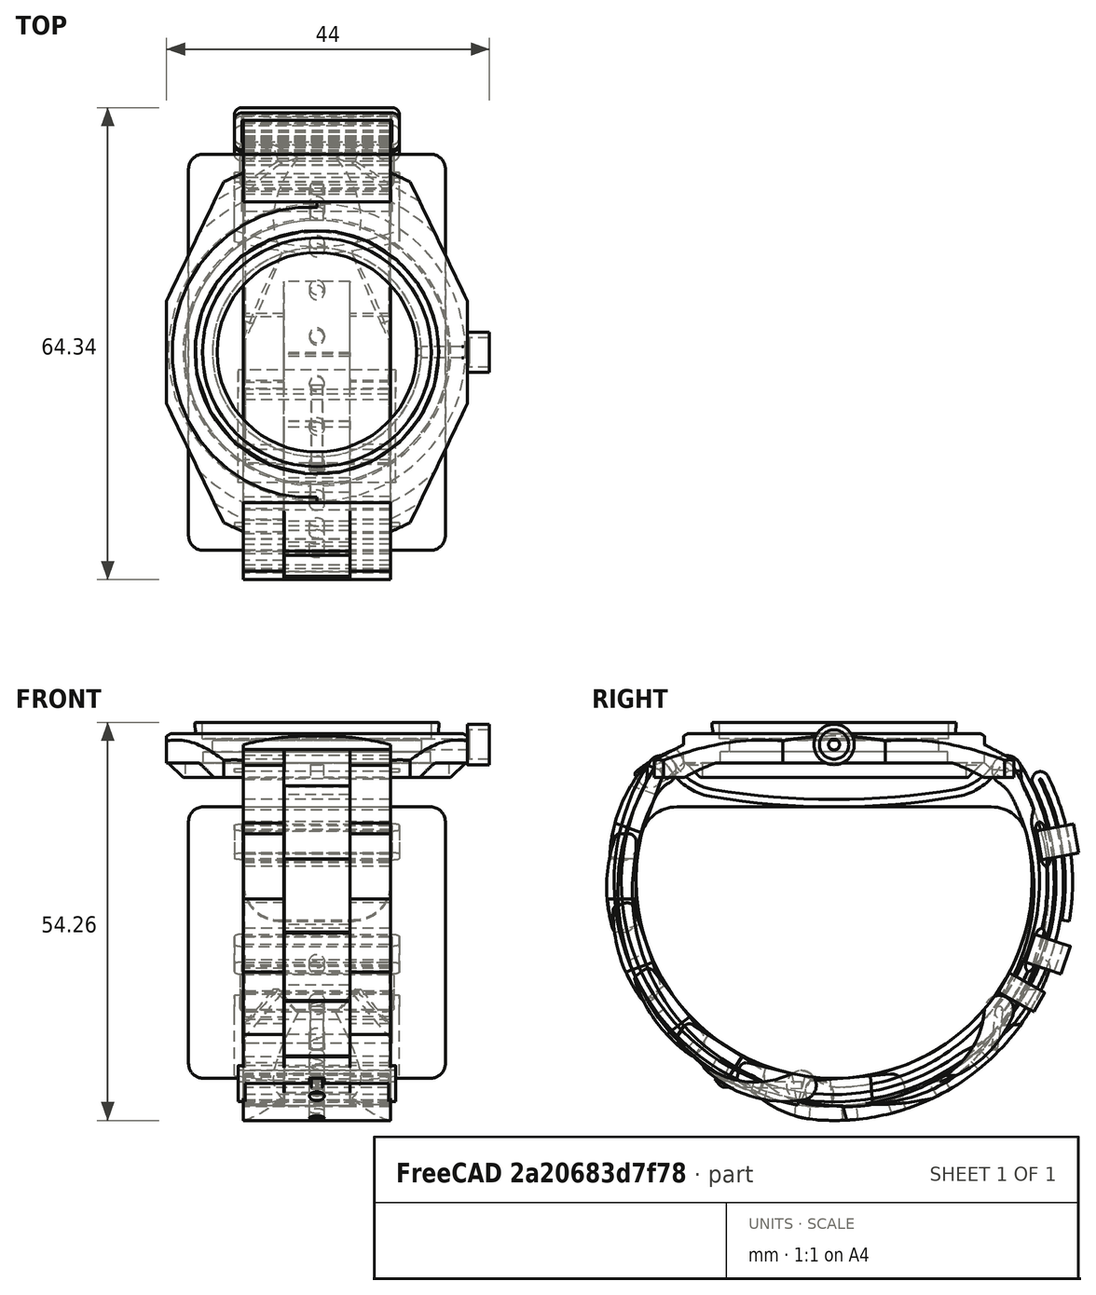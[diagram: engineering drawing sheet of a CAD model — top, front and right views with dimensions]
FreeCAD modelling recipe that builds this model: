
FCSTD DOCUMENT  (FreeCAD 0.19R20415 (Git))
Label: Strap_2
License: All rights reserved
LicenseURL: http://en.wikipedia.org/wiki/All_rights_reserved
objects: Sketcher::SketchObject×36, PartDesign::Pad×14, PartDesign::Body×14, PartDesign::Pocket×11, PartDesign::Plane×7, PartDesign::Fillet×6, PartDesign::SubtractivePipe×5, PartDesign::Mirrored×5, PartDesign::ShapeBinder×3, App::DocumentObjectGroup×3, Mesh::Feature×2, Part::FeaturePython×2, Part::Feature×1, Part::Cylinder×1, Spreadsheet::Sheet×1, PartDesign::Point×1, Part::Cut×1
note: 143 computed .brp shape members not serialized (recipe doc carries the construction recipe); baked Part::Feature solids carry a one-line shape summary decoded from their .brp

FEATURE [Mesh::Feature] hand_01
  Placement = pos=(-135.279,-150.508,-37.6643) rot=(-0.520735,-0.542376,-0.65929;2.00353rad)
FEATURE [Sketcher::SketchObject] Sketch030
  MapMode = 5
  Placement = pos=(0,0,0) rot=(0.57735,0.57735,0.57735;2.0944rad)
  Support = -> [YZ_Plane002]
  sketch-geometry (5):
    g0: ArcOfCircle CenterX=0 CenterY=-10 CenterZ=0 NormalX=0 NormalY=0 NormalZ=1 AngleXU=0 Radius=27 StartAngle=2.91232 EndAngle=6.51246
    g1: GeomPoint X=0 Y=0 Z=0
    g2: LineSegment StartX=-21.4243 StartY=0 StartZ=0 EndX=21.4243 EndY=0 EndZ=0
    g3: ArcOfCircle CenterX=21.4243 CenterY=-5 CenterZ=0 NormalX=0 NormalY=0 NormalZ=1 AngleXU=0 Radius=5 StartAngle=0.229276 EndAngle=1.5708
    g4: ArcOfCircle CenterX=-21.4243 CenterY=-5 CenterZ=0 NormalX=0 NormalY=0 NormalZ=1 AngleXU=0 Radius=5 StartAngle=1.5708 EndAngle=2.91232
  constraints (12):
    c: PointOnObject(g0,g-2)
    c: Coincident(g1,g-1)
    c: Radius(g0) = 27
    c: Horizontal(g2)
    c: PointOnObject(g1,g2)
    c: DistanceY(g0,g1) = 10
    c: Tangent(g0,g3) = -1.5708
    c: Tangent(g2,g3) = 1.5708
    c: Tangent(g0,g4) = -1.5708
    c: Tangent(g2,g4) = 1.5708
    c: Equal(g4,g3)
    c: Radius(g3) = 5
FEATURE [PartDesign::Pad] Pad002
  Length = 35
  Length2 = 100
  Midplane = true
  Placement = pos=(0,0,0) rot=(0.57735,0.57735,0.57735;2.0944rad)
  Profile = -> Sketch030
  Type = 0
FEATURE [Sketcher::SketchObject] Sketch031
  MapMode = 5
  Placement = pos=(0,0,0) rot=(0.57735,0.57735,0.57735;2.0944rad)
  Support = -> [YZ_Plane001]
  expr: Constraints[7] = Spreadsheet.Haut
  expr: Constraints[25] = Spreadsheet.EpaisNato
  expr: Constraints[122] = Spreadsheet.EntreAxe
  sketch-geometry (53):
    g0: ArcOfCircle CenterX=0 CenterY=-10.2233 CenterZ=0 NormalX=0 NormalY=0 NormalZ=1 AngleXU=0 Radius=30 StartAngle=2.56676 EndAngle=5.32325
    g1: ArcOfCircle CenterX=1.77e-14 CenterY=101 CenterZ=0 NormalX=0 NormalY=0 NormalZ=1 AngleXU=0 Radius=100 StartAngle=4.54638 EndAngle=4.8784
    g2: ArcOfCircle CenterX=-23.5 CenterY=5 CenterZ=0 NormalX=0 NormalY=0 NormalZ=1 AngleXU=0 Radius=2 StartAngle=0.526234 EndAngle=2.56676
    g3: ArcOfCircle CenterX=-15.2853 CenterY=9.77166 CenterZ=0 NormalX=0 NormalY=0 NormalZ=1 AngleXU=0 Radius=7.5 StartAngle=3.66783 EndAngle=4.54638
    g4: GeomPoint X=0 Y=1 Z=0
    g5: LineSegment [constr] StartX=17.2073 StartY=-34.7979 StartZ=0 EndX=0 EndY=-10.2233 EndZ=0
    g6: ArcOfCircle CenterX=15.2853 CenterY=9.77166 CenterZ=0 NormalX=0 NormalY=0 NormalZ=1 AngleXU=0 Radius=7.5 StartAngle=4.8784 EndAngle=5.75695
    g7: ArcOfCircle CenterX=23.5 CenterY=5 CenterZ=0 NormalX=0 NormalY=0 NormalZ=1 AngleXU=0 Radius=2 StartAngle=0.574828 EndAngle=2.61536
    g8: ArcOfCircle CenterX=0 CenterY=-10.2233 CenterZ=0 NormalX=0 NormalY=0 NormalZ=1 AngleXU=0 Radius=30 StartAngle=5.62307 EndAngle=6.85801
    g9: ArcOfCircle CenterX=0 CenterY=-10.2233 CenterZ=0 NormalX=0 NormalY=0 NormalZ=1 AngleXU=0 Radius=29 StartAngle=0.347744 EndAngle=0.574828
    g10: LineSegment [constr] StartX=27.2642 StartY=-0.340778 StartZ=0 EndX=28.2043 EndY=0 EndZ=0
    g11: ArcOfCircle CenterX=15.2853 CenterY=9.77166 CenterZ=0 NormalX=0 NormalY=0 NormalZ=1 AngleXU=0 Radius=8.5 StartAngle=4.8784 EndAngle=5.75695
    g12: LineSegment [constr] StartX=16.5247 StartY=2.37477 StartZ=0 EndX=16.6899 EndY=1.38852 EndZ=0
    g13: ArcOfCircle CenterX=1.77e-14 CenterY=101 CenterZ=0 NormalX=0 NormalY=0 NormalZ=1 AngleXU=0 Radius=101 StartAngle=4.54638 EndAngle=4.8784
    g14: ArcOfCircle CenterX=-15.2853 CenterY=9.77166 CenterZ=0 NormalX=0 NormalY=0 NormalZ=1 AngleXU=0 Radius=8.5 StartAngle=3.66783 EndAngle=4.54638
    g15: ArcOfCircle CenterX=-23.5 CenterY=5 CenterZ=0 NormalX=0 NormalY=0 NormalZ=1 AngleXU=0 Radius=1 StartAngle=0.526234 EndAngle=2.56676
    g16: LineSegment [constr] StartX=-16.6899 StartY=1.38852 StartZ=0 EndX=-16.5247 EndY=2.37477 EndZ=0
    g17: LineSegment [constr] StartX=-22.6353 StartY=5.50228 StartZ=0 EndX=-21.7706 EndY=6.00456 EndZ=0
    g18: ArcOfCircle CenterX=0 CenterY=-10.2233 CenterZ=0 NormalX=0 NormalY=0 NormalZ=1 AngleXU=0 Radius=29 StartAngle=2.56676 EndAngle=5.32325
    g19: LineSegment [constr] StartX=-24.3393 StartY=5.54369 StartZ=0 EndX=-25.1786 EndY=6.08738 EndZ=0
    g20: ArcOfCircle CenterX=23.5 CenterY=5 CenterZ=0 NormalX=0 NormalY=0 NormalZ=1 AngleXU=0 Radius=1 StartAngle=0.574828 EndAngle=2.61536
    g21: ArcOfCircle CenterX=0 CenterY=-10.2233 CenterZ=0 NormalX=0 NormalY=0 NormalZ=1 AngleXU=0 Radius=28 StartAngle=5.62307 EndAngle=6.54195
    g22: LineSegment [constr] StartX=22.1178 StartY=-27.3931 StartZ=0 EndX=22.9077 EndY=-28.0063 EndZ=0
    g23: ArcOfCircle CenterX=22.9077 CenterY=-28.0063 CenterZ=0 NormalX=0 NormalY=0 NormalZ=1 AngleXU=0 Radius=1 StartAngle=2.48148 EndAngle=5.62307
    g24: ArcOfCircle CenterX=24.6758 CenterY=-45.4641 CenterZ=0 NormalX=0 NormalY=0 NormalZ=1 AngleXU=0 Radius=14.021 StartAngle=2.01355 EndAngle=2.18166
    g25: ArcOfCircle CenterX=12.0856 CenterY=-18.9105 CenterZ=0 NormalX=0 NormalY=0 NormalZ=1 AngleXU=0 Radius=15.3662 StartAngle=5.15514 EndAngle=5.65995
    g26: ArcOfCircle CenterX=0 CenterY=-10.2233 CenterZ=0 NormalX=0 NormalY=0 NormalZ=1 AngleXU=0 Radius=30.25 StartAngle=5.65995 EndAngle=6.74266
    g27: ArcOfCircle CenterX=28.121 CenterY=3.69067 CenterZ=0 NormalX=0 NormalY=0 NormalZ=1 AngleXU=0 Radius=1.125 StartAngle=0.459471 EndAngle=3.60106
    g28: ArcOfCircle CenterX=0 CenterY=-10.2233 CenterZ=0 NormalX=0 NormalY=0 NormalZ=1 AngleXU=0 Radius=32.5 StartAngle=6.11712 EndAngle=6.74266
    g29: LineSegment [constr] StartX=27.1127 StartY=3.19176 StartZ=0 EndX=29.1293 EndY=4.18958 EndZ=0
    g30: ArcOfCircle CenterX=24.6758 CenterY=-45.4641 CenterZ=0 NormalX=0 NormalY=0 NormalZ=1 AngleXU=0 Radius=13.021 StartAngle=2.01355 EndAngle=2.18166
    g31: ArcOfCircle CenterX=12.0856 CenterY=-18.9105 CenterZ=0 NormalX=0 NormalY=0 NormalZ=1 AngleXU=0 Radius=16.3662 StartAngle=5.15514 EndAngle=5.65995
    g32: ArcOfCircle CenterX=0 CenterY=-10.2233 CenterZ=0 NormalX=0 NormalY=0 NormalZ=1 AngleXU=0 Radius=31.25 StartAngle=5.65995 EndAngle=6.74266
    g33: ArcOfCircle CenterX=28.121 CenterY=3.69067 CenterZ=0 NormalX=0 NormalY=0 NormalZ=1 AngleXU=0 Radius=0.125 StartAngle=0.459471 EndAngle=3.60106
    g34: ArcOfCircle CenterX=0 CenterY=-10.2233 CenterZ=0 NormalX=0 NormalY=0 NormalZ=1 AngleXU=0 Radius=31.5 StartAngle=6.11712 EndAngle=6.74266
    g35: LineSegment StartX=31.0667 StartY=-15.4303 StartZ=0 EndX=32.0529 EndY=-15.5956 EndZ=0
    g36: LineSegment [constr] StartX=28.009 StartY=3.63524 StartZ=0 EndX=27.1127 EndY=3.19176 EndZ=0
    g37: LineSegment [constr] StartX=28.2043 StartY=0 StartZ=0 EndX=28.4394 EndY=0.0851945 EndZ=0
    g38: ArcOfCircle CenterX=31.1215 CenterY=-1.98547 CenterZ=0 NormalX=0 NormalY=0 NormalZ=1 AngleXU=0 Radius=4.19336 StartAngle=2.73856 EndAngle=3.40036
    g39: LineSegment StartX=27.5841 StartY=-3.40486 StartZ=0 EndX=28.2879 EndY=-7.54548 EndZ=0
    g40: LineSegment StartX=28.2879 StartY=-7.54548 StartZ=0 EndX=29.4709 EndY=-7.3444 EndZ=0
    g41: LineSegment StartX=29.4709 StartY=-7.3444 StartZ=0 EndX=28.7671 EndY=-3.20378 EndZ=0
    g42: LineSegment StartX=28.7671 StartY=-3.20378 StartZ=0 EndX=27.5841 EndY=-3.40486 EndZ=0
    g43: LineSegment [constr] StartX=0 StartY=-10.2233 StartZ=0 EndX=29.119 EndY=-5.27409 EndZ=0
    g44: LineSegment StartX=27.5164 StartY=-17.3102 StartZ=0 EndX=26.1711 EndY=-21.289 EndZ=0
    g45: LineSegment StartX=26.1711 StartY=-21.289 StartZ=0 EndX=27.3079 EndY=-21.6733 EndZ=0
    g46: LineSegment StartX=27.3079 StartY=-21.6733 StartZ=0 EndX=28.6531 EndY=-17.6946 EndZ=0
    g47: LineSegment StartX=28.6531 StartY=-17.6946 StartZ=0 EndX=27.5164 EndY=-17.3102 EndZ=0
    g48: LineSegment [constr] StartX=0 StartY=-10.2233 StartZ=0 EndX=27.9805 EndY=-19.684 EndZ=0
    g49: Circle [constr] CenterX=0 CenterY=-10.2233 CenterZ=0 NormalX=0 NormalY=0 NormalZ=1 AngleXU=0 Radius=29.6112
    g50: LineSegment [constr] StartX=29.119 StartY=-5.27409 StartZ=0 EndX=29.5758 EndY=-5.19645 EndZ=0
    g51: LineSegment [constr] StartX=28.7671 StartY=-3.20378 StartZ=0 EndX=29.1514 EndY=-3.13847 EndZ=0
    g52: LineSegment [constr] StartX=27.5841 StartY=-3.40486 StartZ=0 EndX=27.1998 EndY=-3.47017 EndZ=0
  constraints (131):
    c: Symmetric(g1,g1,g-2)
    c: Tangent(g2,g0) = -1.5708
    c: Radius(g2) = 2
    c: Tangent(g1,g3) = -1.5708
    c: Tangent(g3,g2) = 1.5708
    c: Radius(g0) = 30
    c: Radius(g3) = 7.5
    c: DistanceY(g2) = 5
    c: PointOnObject(g4,g1)
    c: PointOnObject(g4,g-2)
    c: Radius(g1) = 100
    c: PointOnObject(g0,g-2)
    c: Coincident(g5,g0)
    c: Coincident(g5,g0)
    c: Angle(g5,g-2) = 2.53073
    c: Tangent(g6,g1) = -1.5708
    c: Symmetric(g6,g2,g-2)
    c: Tangent(g7,g6) = 1.5708
    c: Equal(g7,g2)
    c: Coincident(g8,g0)
    c: Tangent(g8,g7) = -1.5708
    c: Coincident(g9,g0)
    c: Coincident(g10,g9)
    c: PointOnObject(g10,g8)
    c: Perpendicular(g8,g10)
    c: Distance(g10) = 1
    c: Coincident(g12,g1)
    c: Perpendicular(g11,g12)
    c: Equal(g10,g12)
    c: Coincident(g13,g1)
    c: Tangent(g11,g13) = -1.5708
    c: Perpendicular(g6,g12)
    c: Tangent(g13,g14) = -1.5708
    c: Coincident(g16,g13)
    c: Coincident(g16,g1)
    c: Perpendicular(g13,g16)
    c: Equal(g16,g12)
    c: Tangent(g15,g14) = 1.5708
    c: Coincident(g17,g14)
    c: PointOnObject(g17,g3)
    c: Perpendicular(g3,g17)
    c: Equal(g17,g16)
    c: Coincident(g18,g0)
    c: Tangent(g18,g15) = -1.5708
    c: Coincident(g19,g15)
    c: Perpendicular(g0,g19)
    c: Equal(g19,g17)
    c: Coincident(g15,g2)
    c: Coincident(g20,g7)
    c: Tangent(g11,g20) = 1.5708
    c: Tangent(g9,g20) = -1.5708
    c: Coincident(g21,g0)
    c: Coincident(g22,g21)
    c: Equal(g22,g10)
    c: Tangent(g23,g21) = 1.5708
    c: Coincident(g23,g22)
    c: Tangent(g24,g18) = 1.5708
    c: Tangent(g25,g24) = 1.5708
    c: Coincident(g26,g0)
    c: Coincident(g26,g25)
    c: Coincident(g28,g0)
    c: Tangent(g27,g26) = 1.5708
    c: Tangent(g27,g28) = -1.5708
    c: Coincident(g29,g26)
    c: Coincident(g29,g27)
    c: Coincident(g30,g24)
    c: Coincident(g31,g25)
    c: Coincident(g32,g0)
    c: Tangent(g30,g0) = 1.5708
    c: Tangent(g30,g31) = 1.5708
    c: Tangent(g31,g32) = -1.5708
    c: Tangent(g32,g33) = 1.5708
    c: Coincident(g34,g0)
    c: Tangent(g34,g33) = -1.5708
    c: Coincident(g35,g34)
    c: Coincident(g35,g28)
    c: Perpendicular(g34,g35)
    c: Equal(g35,g10)
    c: Coincident(g36,g32)
    c: Perpendicular(g32,g36)
    c: Equal(g36,g10)
    c: Distance(g32,g33) = 0.25
    c: Coincident(g27,g33)
    c: Coincident(g37,g10)
    c: PointOnObject(g37,g26)
    c: Perpendicular(g26,g37)
    c: Distance(g37) = 0.25
    c: Tangent(g38,g21) = 1.5708
    c: Coincident(g9,g38)
    c: Distance(g27,g28) = 20
    c: PointOnObject(g10,g-1)
    c: Tangent(g23,g8) = -1.5708
    c: Coincident(g39,g40)
    c: Coincident(g40,g41)
    c: Coincident(g41,g42)
    c: Coincident(g42,g39)
    c: Perpendicular(g41,g40)
    c: Perpendicular(g41,g42)
    c: Perpendicular(g42,g39)
    c: Distance(g40) = 1.2
    c: Distance(g41) = 4.2
    c: Coincident(g43,g0)
    c: Perpendicular(g43,g41)
    c: Symmetric(g40,g41,g43)
    c: Coincident(g44,g45)
    c: Coincident(g45,g46)
    c: Coincident(g46,g47)
    c: Coincident(g47,g44)
    c: Perpendicular(g46,g45)
    c: Perpendicular(g46,g47)
    c: Perpendicular(g47,g44)
    c: Equal(g40,g45) = 1.2
    c: Equal(g41,g46) = 4.2
    c: Coincident(g48,g0)
    c: Perpendicular(g46,g48)
    c: Symmetric(g45,g46,g48)
    c: Coincident(g49,g0)
    c: PointOnObject(g40,g49)
    c: PointOnObject(g46,g49)
    c: Coincident(g50,g43)
    c: PointOnObject(g50,g8)
    c: Parallel(g50,g43)
    c: DistanceX(g2,g7) = 47
    c: Coincident(g51,g41)
    c: PointOnObject(g51,g8)
    c: Coincident(g52,g39)
    c: PointOnObject(g52,g38)
    c: Parallel(g52,g42)
    c: Parallel(g51,g42)
    c: Equal(g51,g52)
    c: PointOnObject(g-1,g13)
FEATURE [Part::Feature] Body003  label="K-65_Case001"
  shape: bbox 50.12 x 59.75 x 8.013 mm, 71 faces (baked)
FEATURE [PartDesign::Pad] Pad
  Length = 20
  Length2 = 100
  Midplane = true
  Placement = pos=(0,0,0) rot=(0.57735,0.57735,0.57735;2.0944rad)
  Profile = -> Sketch031
  Type = 0
  expr: Length = Spreadsheet.Larg
FEATURE [Sketcher::SketchObject] Sketch
  MapMode = 5
  Placement = pos=(0,0,0) rot=(0.57735,0.57735,0.57735;2.0944rad)
  Support = -> [YZ_Plane]
  expr: Constraints[10] = Spreadsheet.EpaisNato * 3 + 2.1
  sketch-geometry (7):
    g0: LineSegment StartX=27.6094 StartY=-3.26258 StartZ=0 EndX=32.6253 EndY=-2.34006 EndZ=0
    g1: LineSegment StartX=32.6253 StartY=-2.34006 StartZ=0 EndX=33.3488 EndY=-6.27408 EndZ=0
    g2: LineSegment StartX=33.3488 StartY=-6.27408 StartZ=0 EndX=28.333 EndY=-7.19659 EndZ=0
    g3: LineSegment StartX=27.6094 StartY=-3.26258 StartZ=0 EndX=28.333 EndY=-7.19659 EndZ=0
    g4: LineSegment [constr] StartX=27.9712 StartY=-5.22959 StartZ=0 EndX=32.9871 EndY=-4.30707 EndZ=0
    g5: LineSegment [constr] StartX=27.6094 StartY=-3.26258 StartZ=0 EndX=27.5111 EndY=-3.28067 EndZ=0
    g6: LineSegment [constr] StartX=27.6094 StartY=-3.26258 StartZ=0 EndX=27.5913 EndY=-3.16423 EndZ=0
  constraints (17):
    c: Coincident(g0,g1)
    c: Coincident(g1,g2)
    c: Coincident(g0,g3)
    c: Coincident(g3,g2)
    c: Perpendicular(g0,g3)
    c: Perpendicular(g1,g2)
    c: Perpendicular(g0,g1)
    c: Distance(g3) = 4
    c: Symmetric(g0,g1,g4)
    c: Symmetric(g0,g2,g4)
    c: Distance(g2) = 5.1
    c: Coincident(g5,g0)
    c: Coincident(g6,g0)
    c: Parallel(g0,g5)
    c: Parallel(g6,g3)
    c: Equal(g6,g5)
    c: Distance(g6) = 0.1
FEATURE [PartDesign::Pad] Pad003
  Length = 22.5
  Length2 = 100
  Midplane = true
  Placement = pos=(0,0,0) rot=(0.57735,0.57735,0.57735;2.0944rad)
  Profile = -> Sketch
  Type = 0
  expr: Length = Spreadsheet.Larg + 2.5
FEATURE [Sketcher::SketchObject] Sketch032
  ExternalGeometry = -> [Pad003]
  MapMode = 5
  Placement = pos=(2.9e-15,1.48379,-8.06759) rot=(0.090446,0.090446,-0.991786;1.57904rad)
  Support = -> [Pad003]
  sketch-geometry (11):
    g0: LineSegment StartX=-30.4638 StartY=10.25 StartZ=0 EndX=-27.7638 EndY=10.25 EndZ=0
    g1: LineSegment StartX=-27.5638 StartY=10.05 StartZ=0 EndX=-27.5638 EndY=-10.05 EndZ=0
    g2: LineSegment StartX=-27.7638 StartY=-10.25 StartZ=0 EndX=-30.4638 EndY=-10.25 EndZ=0
    g3: LineSegment StartX=-30.6638 StartY=-10.05 StartZ=0 EndX=-30.6638 EndY=10.05 EndZ=0
    g4: GeomPoint X=-29.1138 Y=4.1e-15 Z=0
    g5: ArcOfCircle CenterX=-30.4638 CenterY=10.05 CenterZ=0 NormalX=0 NormalY=0 NormalZ=1 AngleXU=0 Radius=0.2 StartAngle=1.5708 EndAngle=3.14159
    g6: ArcOfCircle CenterX=-27.7638 CenterY=10.05 CenterZ=0 NormalX=0 NormalY=0 NormalZ=1 AngleXU=0 Radius=0.2 StartAngle=-3.6e-15 EndAngle=1.5708
    g7: ArcOfCircle CenterX=-27.7638 CenterY=-10.05 CenterZ=0 NormalX=0 NormalY=0 NormalZ=1 AngleXU=0 Radius=0.2 StartAngle=4.71239 EndAngle=6.28319
    g8: ArcOfCircle CenterX=-30.4638 CenterY=-10.05 CenterZ=0 NormalX=0 NormalY=0 NormalZ=1 AngleXU=0 Radius=0.2 StartAngle=3.14159 EndAngle=4.71239
    g9: LineSegment [constr] StartX=-30.4638 StartY=-10.25 StartZ=0 EndX=-30.4638 EndY=-11.25 EndZ=0
    g10: LineSegment [constr] StartX=-30.6638 StartY=-10.05 StartZ=0 EndX=-31.6638 EndY=-10.05 EndZ=0
  constraints (26):
    c: Horizontal(g0)
    c: Horizontal(g2)
    c: Vertical(g1)
    c: Vertical(g3)
    c: Symmetric(g-4,g-3,g4)
    c: Tangent(g3,g5) = 1.5708
    c: Tangent(g0,g5) = 1.5708
    c: Tangent(g0,g6) = 1.5708
    c: Tangent(g1,g6) = 1.5708
    c: Tangent(g1,g7) = 1.5708
    c: Tangent(g2,g7) = 1.5708
    c: Tangent(g2,g8) = 1.5708
    c: Tangent(g3,g8) = 1.5708
    c: Equal(g8,g7)
    c: Equal(g7,g5)
    c: Equal(g5,g6)
    c: Radius(g5) = 0.2
    c: DistanceY(g-4,g2) = 1
    c: Coincident(g9,g2)
    c: Coincident(g10,g3)
    c: PointOnObject(g10,g-4)
    c: Horizontal(g10)
    c: Horizontal(g9,g-4)
    c: Vertical(g9)
    c: Equal(g10,g9)
    c: Symmetric(g7,g5,g4)
FEATURE [PartDesign::Pocket] Pocket
  BaseFeature = -> Pad003
  Length = 5
  Length2 = 100
  Placement = pos=(0,0,0) rot=(0.57735,0.57735,0.57735;2.0944rad)
  Profile = -> Sketch032
  Type = 0
FEATURE [PartDesign::Fillet] Fillet001
  Base = -> Pocket [Edge18,Edge15,Edge16,Edge14]
  BaseFeature = -> Pocket
  Placement = pos=(0,0,0) rot=(0.57735,0.57735,0.57735;2.0944rad)
  Radius = 1
  SupportTransform = true
FEATURE [PartDesign::Body] Body  label="Nato_Retainer_1"
  Group = -> [Sketch,Pad003,Sketch032,Pocket,Fillet001]
  Origin = -> Origin
  Tip = -> Fillet001
FEATURE [PartDesign::ShapeBinder] ShapeBinder001
  Placement = pos=(10,-4e-15,4e-15) rot=(0,0,1;0rad)
  TraceSupport = false
FEATURE [Sketcher::SketchObject] Sketch033
  ExternalGeometry = -> [ShapeBinder001]
  MapMode = 5
  Placement = pos=(0,0,0) rot=(0.57735,0.57735,0.57735;2.0944rad)
  Support = -> [YZ_Plane003]
  expr: Constraints[7] = Spreadsheet.EpaisNato * 3 + 2.1
  sketch-geometry (6):
    g0: LineSegment StartX=27.3747 StartY=-17.38 StartZ=0 EndX=32.2053 EndY=-19.0156 EndZ=0
    g1: LineSegment StartX=32.2053 StartY=-19.0156 StartZ=0 EndX=30.9226 EndY=-22.8043 EndZ=0
    g2: LineSegment StartX=30.9226 StartY=-22.8043 StartZ=0 EndX=26.0919 EndY=-21.1688 EndZ=0
    g3: LineSegment StartX=26.0919 StartY=-21.1688 StartZ=0 EndX=27.3747 EndY=-17.38 EndZ=0
    g4: LineSegment [constr] StartX=27.3747 StartY=-17.38 StartZ=0 EndX=27.4068 EndY=-17.2853 EndZ=0
    g5: LineSegment [constr] StartX=27.3747 StartY=-17.38 StartZ=0 EndX=27.4694 EndY=-17.4121 EndZ=0
  constraints (18):
    c: Coincident(g0,g1)
    c: Coincident(g1,g2)
    c: Coincident(g2,g3)
    c: Coincident(g3,g0)
    c: Perpendicular(g0,g3)
    c: Perpendicular(g2,g3)
    c: Perpendicular(g1,g2)
    c: Distance(g2) = 5.1
    c: Distance(g3) = 4
    c: Parallel(g3,g-5)
    c: Coincident(g4,g0)
    c: PointOnObject(g4,g-4)
    c: PointOnObject(g5,g-5)
    c: Coincident(g5,g0)
    c: Parallel(g5,g0)
    c: Parallel(g4,g3)
    c: Equal(g4,g5)
    c: Distance(g4) = 0.1
FEATURE [PartDesign::Pad] Pad004
  Length = 22.5
  Length2 = 100
  Midplane = true
  Placement = pos=(0,0,0) rot=(0.57735,0.57735,0.57735;2.0944rad)
  Profile = -> Sketch033
  Type = 0
  expr: Length = Spreadsheet.Larg + 2.5
FEATURE [Sketcher::SketchObject] Sketch034
  ExternalGeometry = -> [Pad004]
  MapMode = 5
  Placement = pos=(9e-16,-2.46397,-7.27759) rot=(-0.1604,-0.1604,-0.973932;1.59721rad)
  Support = -> [Pad004]
  sketch-geometry (11):
    g0: LineSegment StartX=-35.4025 StartY=10.25 StartZ=0 EndX=-32.7025 EndY=10.25 EndZ=0
    g1: LineSegment StartX=-32.5025 StartY=10.05 StartZ=0 EndX=-32.5025 EndY=-10.05 EndZ=0
    g2: LineSegment StartX=-32.7025 StartY=-10.25 StartZ=0 EndX=-35.4025 EndY=-10.25 EndZ=0
    g3: LineSegment StartX=-35.6025 StartY=-10.05 StartZ=0 EndX=-35.6025 EndY=10.05 EndZ=0
    g4: GeomPoint X=-34.0525 Y=5e-15 Z=0
    g5: ArcOfCircle CenterX=-35.4025 CenterY=10.05 CenterZ=0 NormalX=0 NormalY=0 NormalZ=1 AngleXU=0 Radius=0.2 StartAngle=1.5708 EndAngle=3.14159
    g6: ArcOfCircle CenterX=-32.7025 CenterY=10.05 CenterZ=0 NormalX=0 NormalY=0 NormalZ=1 AngleXU=0 Radius=0.2 StartAngle=-4.4e-15 EndAngle=1.5708
    g7: ArcOfCircle CenterX=-32.7025 CenterY=-10.05 CenterZ=0 NormalX=0 NormalY=0 NormalZ=1 AngleXU=0 Radius=0.2 StartAngle=4.71239 EndAngle=6.28319
    g8: ArcOfCircle CenterX=-35.4025 CenterY=-10.05 CenterZ=0 NormalX=0 NormalY=0 NormalZ=1 AngleXU=0 Radius=0.2 StartAngle=3.14159 EndAngle=4.71239
    g9: LineSegment [constr] StartX=-35.4025 StartY=10.25 StartZ=0 EndX=-35.4025 EndY=11.25 EndZ=0
    g10: LineSegment [constr] StartX=-35.6025 StartY=10.05 StartZ=0 EndX=-36.6025 EndY=10.05 EndZ=0
  constraints (26):
    c: Horizontal(g0)
    c: Horizontal(g2)
    c: Vertical(g1)
    c: Vertical(g3)
    c: Tangent(g3,g5) = 1.5708
    c: Tangent(g0,g5) = 1.5708
    c: Tangent(g0,g6) = 1.5708
    c: Tangent(g1,g6) = 1.5708
    c: Tangent(g1,g7) = 1.5708
    c: Tangent(g2,g7) = 1.5708
    c: Tangent(g2,g8) = 1.5708
    c: Tangent(g3,g8) = 1.5708
    c: Equal(g8,g7)
    c: Equal(g7,g5)
    c: Equal(g5,g6)
    c: Radius(g5) = 0.2
    c: Symmetric(g7,g5,g4)
    c: Symmetric(g-5,g-4,g4)
    c: Coincident(g9,g0)
    c: Vertical(g9)
    c: Coincident(g10,g3)
    c: PointOnObject(g10,g-4)
    c: Horizontal(g10)
    c: PointOnObject(g9,g-3)
    c: Equal(g9,g10)
    c: DistanceX(g10,g10) = 1
FEATURE [PartDesign::Pocket] Pocket001
  BaseFeature = -> Pad004
  Length = 5
  Length2 = 100
  Placement = pos=(0,0,0) rot=(0.57735,0.57735,0.57735;2.0944rad)
  Profile = -> Sketch034
  Type = 0
FEATURE [PartDesign::Fillet] Fillet002
  Base = -> Pocket001 [Edge18,Edge15,Edge16,Edge14]
  BaseFeature = -> Pocket001
  Placement = pos=(0,0,0) rot=(0.57735,0.57735,0.57735;2.0944rad)
  Radius = 1
  SupportTransform = true
FEATURE [PartDesign::Body] Body004  label="Nato_Retainer_2"
  Group = -> [ShapeBinder001,Sketch033,Pad004,Sketch034,Pocket001,Fillet002]
  Origin = -> Origin003
  Tip = -> Fillet002
FEATURE [Sketcher::SketchObject] Sketch035
  MapMode = 5
  Placement = pos=(0,0,0) rot=(0.57735,0.57735,0.57735;2.0944rad)
  Support = -> [YZ_Plane004]
  sketch-geometry (7):
    g0: ArcOfCircle CenterX=8.92707 CenterY=-26.8072 CenterZ=0 NormalX=0 NormalY=0 NormalZ=1 AngleXU=0 Radius=11.6054 StartAngle=5.10639 EndAngle=6.21654
    g1: ArcOfCircle CenterX=22.5023 CenterY=-27.7132 CenterZ=0 NormalX=0 NormalY=0 NormalZ=1 AngleXU=0 Radius=2 StartAngle=5.8952 EndAngle=9.35814
    g2: ArcOfCircle CenterX=10.0199 CenterY=-22.6117 CenterZ=0 NormalX=0 NormalY=0 NormalZ=1 AngleXU=0 Radius=15.4846 StartAngle=4.93527 EndAngle=5.8952
    g3: ArcOfCircle CenterX=13.4206 CenterY=-37.6158 CenterZ=0 NormalX=0 NormalY=0 NormalZ=1 AngleXU=0 Radius=0.1 StartAngle=1.96479 EndAngle=4.93527
    g4: GeomPoint X=22.6355 Y=-25.7177 Z=0
    g5: LineSegment [constr] StartX=22.6355 StartY=-25.7177 StartZ=0 EndX=22.5023 EndY=-27.7132 EndZ=0
    g6: LineSegment [constr] StartX=20.5067 StartY=-27.58 StartZ=0 EndX=22.5023 EndY=-27.7132 EndZ=0
  constraints (14):
    c: Tangent(g0,g1) = 1.5708
    c: Tangent(g2,g1) = -1.5708
    c: Tangent(g3,g0) = 1.5708
    c: Tangent(g3,g2) = -1.5708
    c: Radius(g3) = 0.1
    c: Radius(g1) = 2
    c: Angle(g2) = 0.959931
    c: PointOnObject(g4,g1)
    c: Coincident(g5,g4)
    c: Coincident(g5,g1)
    c: Coincident(g6,g0)
    c: Coincident(g6,g1)
    c: Perpendicular(g6,g5)
    c: Distance(g4,g0) = 15
FEATURE [PartDesign::Pad] Pad005
  Length = 22.5
  Length2 = 100
  Midplane = true
  Placement = pos=(0,0,0) rot=(0.57735,0.57735,0.57735;2.0944rad)
  Profile = -> Sketch035
  Type = 0
  expr: Length = Spreadsheet.Larg + 2.5
FEATURE [Sketcher::SketchObject] Sketch036
  ExternalGeometry = -> [Pad005]
  MapMode = 5
  Placement = pos=(0,0,0) rot=(1,0,0;1.5708rad)
  Support = -> [XZ_Plane004]
  sketch-geometry (10):
    g0: LineSegment StartX=-10.25 StartY=-25.58 StartZ=0 EndX=10.25 EndY=-25.58 EndZ=0
    g1: LineSegment StartX=10.25 StartY=-25.58 StartZ=0 EndX=10.25 EndY=-32.2133 EndZ=0
    g2: LineSegment StartX=10.25 StartY=-32.2133 StartZ=0 EndX=-10.25 EndY=-32.2133 EndZ=0
    g3: LineSegment StartX=-10.25 StartY=-32.2133 StartZ=0 EndX=-10.25 EndY=-25.58 EndZ=0
    g4: GeomPoint X=0 Y=-37.7133 Z=0
    g5: ArcOfCircle CenterX=1.18e-14 CenterY=37.5367 CenterZ=0 NormalX=0 NormalY=0 NormalZ=1 AngleXU=0 Radius=75 StartAngle=4.54454 EndAngle=4.88024
    g6: LineSegment StartX=-12.5299 StartY=-36.4092 StartZ=0 EndX=-12.5299 EndY=-40.2207 EndZ=0
    g7: LineSegment StartX=-12.5299 StartY=-40.2207 StartZ=0 EndX=12.5299 EndY=-40.2207 EndZ=0
    g8: LineSegment StartX=12.5299 StartY=-40.2207 StartZ=0 EndX=12.5299 EndY=-36.4092 EndZ=0
    g9: GeomPoint X=0 Y=-37.4633 Z=0
  constraints (24):
    c: Coincident(g0,g1)
    c: Coincident(g1,g2)
    c: Coincident(g2,g3)
    c: Coincident(g3,g0)
    c: Horizontal(g2)
    c: Vertical(g1)
    c: Vertical(g3)
    c: Symmetric(g0,g0,g-2)
    c: DistanceY(g-3,g0) = 2
    c: DistanceY(g-4,g1) = 5.5
    c: DistanceX(g0,g-4) = 1
    c: PointOnObject(g4,g-2)
    c: PointOnObject(g4,g-4)
    c: Coincident(g5,g6)
    c: Coincident(g6,g7)
    c: Coincident(g7,g8)
    c: Coincident(g8,g5)
    c: Vertical(g8)
    c: Symmetric(g5,g5,g-2)
    c: Radius(g5) = 75
    c: Symmetric(g6,g7,g-2)
    c: PointOnObject(g9,g5)
    c: PointOnObject(g9,g-2)
    c: DistanceY(g4,g9) = 0.25
FEATURE [PartDesign::Pocket] Pocket002
  BaseFeature = -> Pad005
  Length = 5
  Length2 = 100
  Placement = pos=(0,0,0) rot=(0.57735,0.57735,0.57735;2.0944rad)
  Profile = -> Sketch036
  Type = 1
FEATURE [Sketcher::SketchObject] Sketch037
  ExternalGeometry = -> [Pocket002]
  MapMode = 5
  Placement = pos=(0,0,0) rot=(0.57735,0.57735,0.57735;2.0944rad)
  Support = -> [YZ_Plane004]
  sketch-geometry (3):
    g0: LineSegment StartX=22.1683 StartY=-32.2133 StartZ=0 EndX=21.4683 EndY=-32.2133 EndZ=0
    g1: ArcOfCircle CenterX=10.0199 CenterY=-22.6117 CenterZ=0 NormalX=0 NormalY=0 NormalZ=1 AngleXU=0 Radius=15.4846 StartAngle=5.54448 EndAngle=5.61435
    g2: LineSegment StartX=21.4683 StartY=-32.2133 StartZ=0 EndX=21.4683 EndY=-33.0381 EndZ=0
  constraints (9):
    c: Coincident(g-4,g0)
    c: PointOnObject(g0,g-4)
    c: Coincident(g1,g0)
    c: Equal(g-3,g1)
    c: PointOnObject(g1,g-3)
    c: Coincident(g2,g0)
    c: Coincident(g2,g1)
    c: Vertical(g2)
    c: DistanceX(g0,g0) = 0.7
FEATURE [PartDesign::Pocket] Pocket003
  BaseFeature = -> Pocket002
  Length = 2
  Length2 = 100
  Midplane = true
  Placement = pos=(0,0,0) rot=(0.57735,0.57735,0.57735;2.0944rad)
  Profile = -> Sketch037
  Type = 0
FEATURE [PartDesign::Body] Body005  label="Nato_Buckle_1"
  Group = -> [Sketch035,Pad005,Sketch036,Pocket002,Sketch037,Pocket003]
  Origin = -> Origin004
  Tip = -> Pocket003
FEATURE [PartDesign::ShapeBinder] ShapeBinder003
  Support = -> [Pocket003]
  TraceSupport = false
FEATURE [Sketcher::SketchObject] Sketch038
  ExternalGeometry = -> [ShapeBinder003]
  MapMode = 5
  Placement = pos=(0,0,0) rot=(0.57735,0.57735,0.57735;2.0944rad)
  Support = -> [YZ_Plane005]
  sketch-geometry (8):
    g0: LineSegment StartX=23.0003 StartY=-27.7583 StartZ=0 EndX=22.2393 EndY=-32.9709 EndZ=0
    g1: LineSegment StartX=21.9694 StartY=-33.1838 StartZ=0 EndX=21.5589 EndY=-33.1467 EndZ=0
    g2: LineSegment StartX=21.5136 StartY=-33.0924 StartZ=0 EndX=22.0043 EndY=-27.6682 EndZ=0
    g3: ArcOfCircle CenterX=22.5023 CenterY=-27.7132 CenterZ=0 NormalX=0 NormalY=0 NormalZ=1 AngleXU=0 Radius=0.5 StartAngle=6.19296 EndAngle=9.33455
    g4: LineSegment [constr] StartX=22.3401 StartY=-32.2809 StartZ=0 EndX=21.5931 EndY=-32.2133 EndZ=0
    g5: ArcOfCircle CenterX=21.5634 CenterY=-33.0969 CenterZ=0 NormalX=0 NormalY=0 NormalZ=1 AngleXU=0 Radius=0.05 StartAngle=3.05136 EndAngle=4.62216
    g6: LineSegment [constr] StartX=21.4683 StartY=-33.0381 StartZ=0 EndX=21.5181 EndY=-33.0426 EndZ=0
    g7: ArcOfCircle CenterX=21.992 CenterY=-32.9348 CenterZ=0 NormalX=0 NormalY=0 NormalZ=1 AngleXU=0 Radius=0.25 StartAngle=4.62216 EndAngle=6.13823
  constraints (22):
    c: Tangent(g2,g3) = 1.5708
    c: Coincident(g3,g0)
    c: Distance(g2,g0) = 1
    c: PointOnObject(g4,g2)
    c: Perpendicular(g2,g4)
    c: Distance(g4) = 0.75
    c: Tangent(g2,g5) = 1.5708
    c: Tangent(g1,g5) = 1.5708
    c: Radius(g5) = 0.05
    c: Coincident(g6,g-4)
    c: PointOnObject(g6,g2)
    c: Perpendicular(g6,g2)
    c: Distance(g6) = 0.05
    c: Distance(g6,g2) = 0.05
    c: Coincident(g3,g-6)
    c: Symmetric(g2,g0,g3)
    c: PointOnObject(g4,g-5)
    c: Perpendicular(g2,g1)
    c: Tangent(g0,g7) = 1.5708
    c: Tangent(g1,g7) = 1.5708
    c: Radius(g7) = 0.25
    c: PointOnObject(g4,g0)
FEATURE [PartDesign::Pad] Pad006
  Length = 1.8
  Length2 = 100
  Midplane = true
  Placement = pos=(0,0,0) rot=(0.57735,0.57735,0.57735;2.0944rad)
  Profile = -> Sketch038
  Type = 0
FEATURE [PartDesign::Fillet] Fillet003
  Base = -> Pad006 [Edge16,Edge15]
  BaseFeature = -> Pad006
  Placement = pos=(0,0,0) rot=(0.57735,0.57735,0.57735;2.0944rad)
  Radius = 0.3
  SupportTransform = true
FEATURE [PartDesign::Body] Body006  label="Nato_Buckle_2"
  Group = -> [ShapeBinder003,Sketch038,Pad006,Fillet003]
  Origin = -> Origin005
  Tip = -> Fillet003
FEATURE [PartDesign::Fillet] Fillet004
  Base = -> Pad002 [Edge7,Edge6]
  BaseFeature = -> Pad002
  Placement = pos=(0,0,0) rot=(0.57735,0.57735,0.57735;2.0944rad)
  Radius = 2
  SupportTransform = false
FEATURE [PartDesign::Body] Body002  label="Arm"
  Group = -> [Sketch030,Pad002,Fillet004]
  Origin = -> Origin002
  Tip = -> Fillet004
FEATURE [Sketcher::SketchObject] Sketch039
  MapMode = 5
  Placement = pos=(0,0,0) rot=(0.57735,0.57735,0.57735;2.0944rad)
  Support = -> [YZ_Plane001]
  sketch-geometry (29):
    g0: LineSegment StartX=27.4949 StartY=-3.10402 StartZ=0 EndX=28.2442 EndY=-7.23664 EndZ=0
    g1: ArcOfCircle CenterX=28.6101 CenterY=-2.90183 CenterZ=0 NormalX=0 NormalY=0 NormalZ=1 AngleXU=0 Radius=1.13333 StartAngle=2.24011 EndAngle=3.32095
    g2: ArcOfCircle CenterX=27.5605 CenterY=-3.09212 CenterZ=0 NormalX=0 NormalY=0 NormalZ=1 AngleXU=0 Radius=1.13333 StartAngle=0.179361 EndAngle=1.2602
    g3: GeomPoint X=28.0853 Y=-2.99698 Z=0
    g4: LineSegment StartX=29.425 StartY=-7.02256 StartZ=0 EndX=28.6757 EndY=-2.88994 EndZ=0
    g5: ArcOfCircle CenterX=28.2503 CenterY=-7.23554 CenterZ=0 NormalX=0 NormalY=0 NormalZ=1 AngleXU=0 Radius=1.19386 StartAngle=5.46137 EndAngle=6.46255
    g6: ArcOfCircle CenterX=29.4189 CenterY=-7.02365 CenterZ=0 NormalX=0 NormalY=0 NormalZ=1 AngleXU=0 Radius=1.19386 StartAngle=3.32095 EndAngle=4.32213
    g7: GeomPoint X=28.8346 Y=-7.1296 Z=0
    g8: LineSegment [constr] StartX=27.9069 StartY=-2.01302 StartZ=0 EndX=28.0853 EndY=-2.99698 EndZ=0
    g9: LineSegment [constr] StartX=28.8346 StartY=-7.1296 StartZ=0 EndX=29.013 EndY=-8.11356 EndZ=0
    g10: LineSegment StartX=26.1546 StartY=-21.2956 StartZ=0 EndX=27.5015 EndY=-17.3174 EndZ=0
    g11: LineSegment StartX=28.6381 StartY=-17.7022 StartZ=0 EndX=27.2912 EndY=-21.6804 EndZ=0
    g12: ArcOfCircle CenterX=28.6323 CenterY=-17.7003 CenterZ=0 NormalX=0 NormalY=0 NormalZ=1 AngleXU=0 Radius=1.19386 StartAngle=1.81396 EndAngle=2.81514
    g13: ArcOfCircle CenterX=27.5073 CenterY=-17.3194 CenterZ=0 NormalX=0 NormalY=0 NormalZ=1 AngleXU=0 Radius=1.19386 StartAngle=5.95673 EndAngle=6.95791
    g14: ArcOfCircle CenterX=27.2854 CenterY=-21.6784 CenterZ=0 NormalX=0 NormalY=0 NormalZ=1 AngleXU=0 Radius=1.19386 StartAngle=2.81514 EndAngle=3.81632
    g15: ArcOfCircle CenterX=26.1604 CenterY=-21.2975 CenterZ=0 NormalX=0 NormalY=0 NormalZ=1 AngleXU=0 Radius=1.19386 StartAngle=4.95555 EndAngle=5.95673
    g16: GeomPoint X=28.0698 Y=-17.5098 Z=0
    g17: GeomPoint X=26.7229 Y=-21.488 Z=0
    g18: LineSegment [constr] StartX=28.3905 StartY=-16.5626 StartZ=0 EndX=28.0698 EndY=-17.5098 EndZ=0
    g19: LineSegment [constr] StartX=26.7229 StartY=-21.488 StartZ=0 EndX=26.4022 EndY=-22.4352 EndZ=0
    g20: ArcOfCircle CenterX=1.1e-15 CenterY=-10.2233 CenterZ=0 NormalX=0 NormalY=0 NormalZ=1 AngleXU=0 Radius=29.1399 StartAngle=6.0635 EndAngle=6.35578
    g21: LineSegment [constr] StartX=1.1e-15 StartY=-10.2233 StartZ=0 EndX=29.0632 EndY=-8.10991 EndZ=0
    g22: LineSegment [constr] StartX=28.4395 StartY=-16.5736 StartZ=0 EndX=0 EndY=-10.2233 EndZ=0
    g23: ArcOfCircle CenterX=1.1e-15 CenterY=-10.2233 CenterZ=0 NormalX=0 NormalY=0 NormalZ=1 AngleXU=0 Radius=29.0405 StartAngle=6.06387 EndAngle=6.35541
    g24: ArcOfCircle CenterX=1.1e-15 CenterY=-10.2233 CenterZ=0 NormalX=0 NormalY=0 NormalZ=1 AngleXU=0 Radius=29.1399 StartAngle=5.63741 EndAngle=5.84996
    g25: LineSegment [constr] StartX=26.4478 StartY=-22.4563 StartZ=0 EndX=0 EndY=-10.2233 EndZ=0
    g26: ArcOfCircle CenterX=1.1e-15 CenterY=-10.2233 CenterZ=0 NormalX=0 NormalY=0 NormalZ=1 AngleXU=0 Radius=29.0405 StartAngle=5.63741 EndAngle=5.84959
    g27: LineSegment StartX=23.1927 StartY=-27.7003 StartZ=0 EndX=23.2722 EndY=-27.7602 EndZ=0
    g28: LineSegment [constr] StartX=23.1927 StartY=-27.7003 StartZ=0 EndX=0 EndY=-10.2233 EndZ=0
  constraints (53):
    c: Tangent(g0,g1) = -1.5708
    c: Coincident(g2,g1)
    c: Symmetric(g2,g1,g3)
    c: Coincident(g4,g2)
    c: Coincident(g5,g4)
    c: Coincident(g6,g0)
    c: Symmetric(g0,g4,g7)
    c: Symmetric(g6,g5,g7)
    c: Coincident(g8,g1)
    c: Coincident(g8,g3)
    c: Coincident(g9,g7)
    c: Equal(g9,g8)
    c: Distance(g8) = 1
    c: Coincident(g12,g10)
    c: Coincident(g13,g11)
    c: Coincident(g14,g10)
    c: Coincident(g15,g11)
    c: Symmetric(g10,g11,g17)
    c: Symmetric(g14,g15,g17)
    c: Symmetric(g13,g12,g16)
    c: Coincident(g18,g16)
    c: Coincident(g19,g17)
    c: Equal(g18,g19)
    c: Symmetric(g10,g11,g16)
    c: Distance(g18) = 1
    c: Coincident(g23,g20)
    c: Coincident(g5,g20)
    c: Coincident(g13,g20)
    c: Coincident(g24,g20)
    c: Coincident(g15,g24)
    c: Symmetric(g15,g14,g19)
    c: Distance(g14,g15) = 0.1
    c: PointOnObject(g18,g22)
    c: Coincident(g12,g23)
    c: Symmetric(g13,g12,g18)
    c: Coincident(g13,g22)
    c: Symmetric(g23,g5,g9)
    c: Coincident(g6,g23)
    c: Coincident(g21,g5)
    c: Distance(g6,g5) = 0.1
    c: Coincident(g21,g20)
    c: Coincident(g21,g22)
    c: Coincident(g25,g15)
    c: Coincident(g25,g20)
    c: PointOnObject(g19,g25)
    c: Coincident(g26,g20)
    c: Coincident(g26,g14)
    c: Coincident(g27,g26)
    c: Coincident(g27,g24)
    c: Perpendicular(g26,g27)
    c: Coincident(g28,g26)
    c: Coincident(g28,g20)
    c: Angle(g28,g-2) = 2.21657
FEATURE [PartDesign::Pocket] Pocket004
  BaseFeature = -> Pad
  Length = 5
  Length2 = 100
  Midplane = true
  Placement = pos=(0,0,0) rot=(0.57735,0.57735,0.57735;2.0944rad)
  Profile = -> Sketch039
  Type = 1
FEATURE [Sketcher::SketchObject] Sketch041
  MapMode = 5
  Placement = pos=(0,0,0) rot=(0.57735,0.57735,0.57735;2.0944rad)
  Support = -> [YZ_Plane006]
  expr: Constraints[39] = -Spreadsheet.EntreAxe / 2
  expr: Constraints[29] = Spreadsheet.EpaisLeather
  expr: Constraints[26] = Spreadsheet.Haut
  expr: Constraints[24] = Spreadsheet.EpaisLeather
  sketch-geometry (18):
    g0: ArcOfCircle CenterX=0 CenterY=-11.4924 CenterZ=0 NormalX=0 NormalY=0 NormalZ=1 AngleXU=0 Radius=29.5 StartAngle=2.65061 EndAngle=4.27606
    g1: LineSegment [constr] StartX=-12.4672 StartY=-38.2285 StartZ=0 EndX=0 EndY=-11.4924 EndZ=0
    g2: ArcOfCircle CenterX=0 CenterY=-11.4924 CenterZ=0 NormalX=0 NormalY=0 NormalZ=1 AngleXU=0 Radius=27.5 StartAngle=2.65061 EndAngle=4.27606
    g3: ArcOfCircle CenterX=-17.9613 CenterY=-50.0105 CenterZ=0 NormalX=0 NormalY=0 NormalZ=1 AngleXU=0 Radius=15 StartAngle=0.910712 EndAngle=1.13446
    g4: ArcOfCircle CenterX=-1.31155 CenterY=-28.5613 CenterZ=0 NormalX=0 NormalY=0 NormalZ=1 AngleXU=0 Radius=12.1529 StartAngle=4.0523 EndAngle=4.6357
    g5: ArcOfCircle CenterX=0 CenterY=-11.4924 CenterZ=0 NormalX=0 NormalY=0 NormalZ=1 AngleXU=0 Radius=29.2721 StartAngle=4.6357 EndAngle=5.93412
    g6: ArcOfCircle CenterX=28.4465 CenterY=-21.8461 CenterZ=0 NormalX=0 NormalY=0 NormalZ=1 AngleXU=0 Radius=1 StartAngle=5.93412 EndAngle=9.07571
    g7: ArcOfCircle CenterX=-17.9613 CenterY=-50.0105 CenterZ=0 NormalX=0 NormalY=0 NormalZ=1 AngleXU=0 Radius=13 StartAngle=0.910712 EndAngle=1.13446
    g8: ArcOfCircle CenterX=-1.31155 CenterY=-28.5613 CenterZ=0 NormalX=0 NormalY=0 NormalZ=1 AngleXU=0 Radius=14.1529 StartAngle=4.0523 EndAngle=4.6357
    g9: ArcOfCircle CenterX=0 CenterY=-11.4924 CenterZ=0 NormalX=0 NormalY=0 NormalZ=1 AngleXU=0 Radius=31.2721 StartAngle=4.6357 EndAngle=5.93412
    g10: LineSegment [constr] StartX=-8.76353 StartY=-38.1614 StartZ=0 EndX=0 EndY=-11.4924 EndZ=0
    g11: LineSegment [constr] StartX=-2.24262 StartY=-40.6785 StartZ=0 EndX=0 EndY=-11.4924 EndZ=0
    g12: LineSegment [constr] StartX=0 StartY=-11.4924 StartZ=0 EndX=28.4465 EndY=-21.8461 EndZ=0
    g13: ArcOfCircle CenterX=-23.5 CenterY=5 CenterZ=0 NormalX=0 NormalY=0 NormalZ=1 AngleXU=0 Radius=2 StartAngle=5.23013 EndAngle=9.49587
    g14: ArcOfCircle CenterX=-29.9836 CenterY=4.53832 CenterZ=0 NormalX=0 NormalY=0 NormalZ=1 AngleXU=0 Radius=4.5 StartAngle=5.7922 EndAngle=6.35427
    g15: ArcOfCircle CenterX=-20.283 CenterY=-0.648096 CenterZ=0 NormalX=0 NormalY=0 NormalZ=1 AngleXU=0 Radius=4.5 StartAngle=2.08854 EndAngle=2.65061
    g16: LineSegment [constr] StartX=-24.2514 StartY=1.47362 StartZ=0 EndX=-26.0152 EndY=2.4166 EndZ=0
    g17: LineSegment [constr] StartX=-29.9836 StartY=4.53832 StartZ=0 EndX=-20.283 EndY=-0.648096 EndZ=0
  constraints (42):
    c: PointOnObject(g0,g-2)
    c: Coincident(g1,g0)
    c: Coincident(g1,g0)
    c: Coincident(g2,g0)
    c: Tangent(g3,g2) = 1.5708
    c: Tangent(g4,g3) = 1.5708
    c: Coincident(g5,g0)
    c: Coincident(g7,g3)
    c: Coincident(g8,g4)
    c: Coincident(g9,g0)
    c: Tangent(g7,g0) = 1.5708
    c: Tangent(g7,g8) = 1.5708
    c: Tangent(g8,g9) = -1.5708
    c: Tangent(g6,g9) = -1.5708
    c: Coincident(g10,g3)
    c: Coincident(g10,g0)
    c: Radius(g3) = 15
    c: Coincident(g11,g4)
    c: Coincident(g11,g0)
    c: Coincident(g12,g0)
    c: Coincident(g12,g6)
    c: Angle(g12,g-2) = 1.91986
    c: Radius(g0) = 29.5
    c: Angle(g-2,g1) = 2.70526
    c: Radius(g13) = 2
    c: Equal(g15,g14)
    c: DistanceY(g13) = 5
    c: PointOnObject(g16,g0)
    c: Perpendicular(g0,g16)
    c: Distance(g16) = 2
    c: Tangent(g13,g14) = 1.5708
    c: Tangent(g14,g0) = 1.5708
    c: Radius(g15) = 4.5
    c: Coincident(g17,g14)
    c: Coincident(g17,g15)
    c: Perpendicular(g0,g17)
    c: Tangent(g2,g15) = -1.5708
    c: Coincident(g2,g16)
    c: Tangent(g13,g15) = 1.5708
    c: DistanceX(g13) = -23.5
    c: Tangent(g5,g4) = -1.5708
    c: Tangent(g6,g5) = 1.5708
FEATURE [PartDesign::Pad] Pad007
  Length = 20
  Length2 = 100
  Midplane = true
  Placement = pos=(0,0,0) rot=(0.57735,0.57735,0.57735;2.0944rad)
  Profile = -> Sketch041
  Type = 0
  expr: Length = Spreadsheet.Larg
FEATURE [Part::Cylinder] Cylinder  label="Cylindre"
  Angle = 360
  AttacherType = Attacher::AttachEngine3D
  Height = 15
  Placement = pos=(0,24.4584,-39.1372) rot=(-1,0,0;5.49779rad)
  Radius = 1
FEATURE [Part::FeaturePython] Array  # Draft array (typed FeaturePython)
  Angle = -110
  ArrayType = 1
  Axis = (1,0,0)
  Base = -> Cylinder
  Center = (0,0,-11.5)
  Fuse = false
  IntervalAxis = (0,0,0)
  IntervalX = (1,0,0)
  IntervalY = (0,1,0)
  IntervalZ = (0,0,1)
  NumberCircles = 2
  NumberPolar = 10
  NumberX = 1
  NumberY = 1
  NumberZ = 1
  RadialDistance = 1
  Symmetry = 1
  TangentialDistance = 1
FEATURE [Sketcher::SketchObject] Sketch048
  MapMode = 5
  Placement = pos=(0,0,0) rot=(0.57735,0.57735,0.57735;2.0944rad)
  Support = -> [YZ_Plane007]
  sketch-geometry (7):
    g0: ArcOfCircle CenterX=-10.7931 CenterY=-25.9402 CenterZ=0 NormalX=0 NormalY=0 NormalZ=1 AngleXU=0 Radius=11.5959 StartAngle=4.08813 EndAngle=5.19928
    g1: ArcOfCircle CenterX=-4.43191 CenterY=-37.9562 CenterZ=0 NormalX=0 NormalY=0 NormalZ=1 AngleXU=0 Radius=2 StartAngle=4.88438 EndAngle=8.34087
    g2: ArcOfCircle CenterX=-6.74905 CenterY=-24.6166 CenterZ=0 NormalX=0 NormalY=0 NormalZ=1 AngleXU=0 Radius=15.5393 StartAngle=3.92445 EndAngle=4.88438
    g3: ArcOfCircle CenterX=-17.6586 CenterY=-35.4708 CenterZ=0 NormalX=0 NormalY=0 NormalZ=1 AngleXU=0 Radius=0.15 StartAngle=0.946533 EndAngle=3.92445
    g4: GeomPoint X=-2.66433 Y=-37.0204 Z=0
    g5: LineSegment [constr] StartX=-2.66433 StartY=-37.0204 StartZ=0 EndX=-4.43191 EndY=-37.9562 EndZ=0
    g6: LineSegment [constr] StartX=-5.36767 StartY=-36.1886 StartZ=0 EndX=-4.43191 EndY=-37.9562 EndZ=0
  constraints (14):
    c: Tangent(g0,g1) = 1.5708
    c: Tangent(g2,g1) = -1.5708
    c: Tangent(g3,g0) = 1.5708
    c: Tangent(g3,g2) = -1.5708
    c: Radius(g3) = 0.15
    c: Radius(g1) = 2
    c: Angle(g2) = 0.959931
    c: PointOnObject(g4,g1)
    c: Coincident(g5,g4)
    c: Coincident(g5,g1)
    c: Coincident(g6,g0)
    c: Coincident(g6,g1)
    c: Perpendicular(g6,g5)
    c: Distance(g4,g0) = 15
FEATURE [PartDesign::Pad] Pad008
  Length = 21.5
  Length2 = 100
  Midplane = true
  Placement = pos=(0,0,0) rot=(0.57735,0.57735,0.57735;2.0944rad)
  Profile = -> Sketch048
  Type = 0
  expr: Length = Spreadsheet.Larg + 1.5
FEATURE [PartDesign::Plane] DatumPlane004
  Length = 71.4053
  MapMode = 6
  Placement = pos=(10.75,-4.08963,-39.9267) rot=(0.705797,0.705797,0.060844;3.26313rad)
  ResizeMode = 0
  Support = -> [Pad008]
  Width = 60.9921
FEATURE [Sketcher::SketchObject] Sketch049
  AttachmentOffset = pos=(0,0,0) rot=(0,0,1;1.5708rad)
  ExternalGeometry = -> [Pad008]
  MapMode = 5
  Placement = pos=(10.75,-4.08963,-39.9267) rot=(1,0,0;3.31358rad)
  Support = -> [DatumPlane004]
  sketch-geometry (5):
    g0: LineSegment StartX=-20.5 StartY=10.5089 StartZ=0 EndX=-1 EndY=10.5089 EndZ=0
    g1: LineSegment StartX=-1 StartY=10.5089 StartZ=0 EndX=-1 EndY=1 EndZ=0
    g2: LineSegment StartX=-1 StartY=1 StartZ=0 EndX=-20.5 EndY=1 EndZ=0
    g3: LineSegment StartX=-20.5 StartY=1 StartZ=0 EndX=-20.5 EndY=10.5089 EndZ=0
    g4: LineSegment [constr] StartX=-10.75 StartY=12.7291 StartZ=0 EndX=-10.75 EndY=0 EndZ=0
  constraints (14):
    c: Coincident(g0,g1)
    c: Coincident(g1,g2)
    c: Coincident(g2,g3)
    c: Coincident(g3,g0)
    c: Horizontal(g0)
    c: Horizontal(g2)
    c: Vertical(g1)
    c: Vertical(g3)
    c: PointOnObject(g4,g-1)
    c: Symmetric(g-3,g-3,g4)
    c: Symmetric(g0,g0,g4)
    c: DistanceX(g0,g-3) = 1
    c: DistanceY(g-1,g1) = 1
    c: DistanceX(g0,g0) = 19.5
FEATURE [PartDesign::Pocket] Pocket006
  BaseFeature = -> Pad008
  Length = 5
  Length2 = 100
  Placement = pos=(0,0,0) rot=(0.57735,0.57735,0.57735;2.0944rad)
  Profile = -> Sketch049
  Type = 1
FEATURE [Sketcher::SketchObject] Sketch050
  MapMode = 5
  Placement = pos=(0,0,0) rot=(0.57735,0.57735,0.57735;2.0944rad)
  Support = -> [YZ_Plane007]
  sketch-geometry (4):
    g0: LineSegment StartX=-16.4907 StartY=-37.4948 StartZ=0 EndX=-15.9365 EndY=-36.7558 EndZ=0
    g1: LineSegment StartX=-15.9365 StartY=-36.7558 StartZ=0 EndX=-13.4938 EndY=-38.4595 EndZ=0
    g2: LineSegment StartX=-16.4907 StartY=-37.4948 StartZ=0 EndX=-14.5201 EndY=-39.3011 EndZ=0
    g3: LineSegment StartX=-14.5201 StartY=-39.3011 StartZ=0 EndX=-13.4938 EndY=-38.4595 EndZ=0
  constraints (4):
    c: Coincident(g0,g1)
    c: Coincident(g0,g2)
    c: Coincident(g2,g3)
    c: Coincident(g3,g1)
FEATURE [PartDesign::Pocket] Pocket007
  BaseFeature = -> Pocket006
  Length = 2
  Length2 = 100
  Midplane = true
  Placement = pos=(0,0,0) rot=(0.57735,0.57735,0.57735;2.0944rad)
  Profile = -> Sketch050
  Type = 0
FEATURE [PartDesign::Body] Body008  label="Leather_Buckle_1"
  Group = -> [Sketch048,Pad008,Sketch049,DatumPlane004,Pocket006,Sketch050,Pocket007]
  Origin = -> Origin007
  Tip = -> Pocket007
FEATURE [PartDesign::ShapeBinder] ShapeBinder004
  Placement = pos=(10.75,-1e-14,7e-15) rot=(0,0,1;0rad)
  Support = -> [Pocket007]
  TraceSupport = false
FEATURE [Sketcher::SketchObject] Sketch051
  ExternalGeometry = -> [ShapeBinder004]
  MapMode = 5
  Placement = pos=(0,0,0) rot=(0.57735,0.57735,0.57735;2.0944rad)
  Support = -> [YZ_Plane008]
  sketch-geometry (8):
    g0: LineSegment StartX=-16.1455 StartY=-37.1566 StartZ=0 EndX=-15.9142 EndY=-36.8378 EndZ=0
    g1: LineSegment StartX=-15.9142 StartY=-36.8378 StartZ=0 EndX=-15.0336 EndY=-37.4019 EndZ=0
    g2: LineSegment StartX=-15.0336 StartY=-37.4019 StartZ=0 EndX=-4.43191 EndY=-37.4562 EndZ=0
    g3: LineSegment StartX=-4.43191 StartY=-37.4562 StartZ=0 EndX=-4.43191 EndY=-38.4562 EndZ=0
    g4: LineSegment StartX=-4.43191 StartY=-38.4562 StartZ=0 EndX=-15.0026 EndY=-38.2167 EndZ=0
    g5: LineSegment StartX=-15.4778 StartY=-38.0095 StartZ=0 EndX=-16.1327 EndY=-37.335 EndZ=0
    g6: ArcOfCircle CenterX=-14.9871 CenterY=-37.533 CenterZ=0 NormalX=0 NormalY=0 NormalZ=1 AngleXU=0 Radius=0.6839 StartAngle=3.91229 EndAngle=4.68974
    g7: ArcOfCircle CenterX=-16.033 CenterY=-37.2382 CenterZ=0 NormalX=0 NormalY=0 NormalZ=1 AngleXU=0 Radius=0.13896 StartAngle=2.51391 EndAngle=3.91229
  constraints (11):
    c: Coincident(g0,g1)
    c: Coincident(g1,g2)
    c: Coincident(g2,g3)
    c: Vertical(g3)
    c: Coincident(g3,g4)
    c: Distance(g3) = 1
    c: Tangent(g5,g6) = 1.5708
    c: Tangent(g4,g6) = 1.5708
    c: Tangent(g0,g7) = 1.5708
    c: Tangent(g5,g7) = 1.5708
    c: Symmetric(g2,g3,g-3)
FEATURE [PartDesign::Pad] Pad009
  Length = 1.5
  Length2 = 100
  Midplane = true
  Placement = pos=(0,0,0) rot=(0.57735,0.57735,0.57735;2.0944rad)
  Profile = -> Sketch051
  Type = 0
FEATURE [PartDesign::Body] Body009  label="Leather_Buckle_2"
  Group = -> [Sketch051,Pad009,ShapeBinder004]
  Origin = -> Origin008
  Tip = -> Pad009
FEATURE [Sketcher::SketchObject] Sketch052
  MapMode = 5
  Placement = pos=(0,0,0) rot=(0.57735,0.57735,0.57735;2.0944rad)
  Support = -> [YZ_Plane009]
  expr: Constraints[2] = Spreadsheet.Haut
  expr: Constraints[1] = Spreadsheet.EntreAxe / 2
  expr: Constraints[17] = Spreadsheet.EpaisLeather
  expr: Constraints[0] = Spreadsheet.EpaisLeather
  sketch-geometry (9):
    g0: ArcOfCircle CenterX=23.5 CenterY=5 CenterZ=0 NormalX=0 NormalY=0 NormalZ=1 AngleXU=0 Radius=2 StartAngle=6.21437 EndAngle=10.4382
    g1: ArcOfCircle CenterX=19.7971 CenterY=-0.940399 CenterZ=0 NormalX=0 NormalY=0 NormalZ=1 AngleXU=0 Radius=5 StartAngle=0.472288 EndAngle=1.01339
    g2: ArcOfCircle CenterX=0 CenterY=-11.0537 CenterZ=0 NormalX=0 NormalY=0 NormalZ=1 AngleXU=0 Radius=27.2307 StartAngle=4.74227 EndAngle=6.75547
    g3: ArcOfCircle CenterX=0.664193 CenterY=-33.2744 CenterZ=0 NormalX=0 NormalY=0 NormalZ=1 AngleXU=0 Radius=5 StartAngle=3.88267 EndAngle=4.74227
    g4: ArcOfCircle CenterX=-4.5 CenterY=-38 CenterZ=0 NormalX=0 NormalY=0 NormalZ=1 AngleXU=0 Radius=2 StartAngle=0.741077 EndAngle=4.73838
    g5: ArcOfCircle CenterX=30.4834 CenterY=4.5187 CenterZ=0 NormalX=0 NormalY=0 NormalZ=1 AngleXU=0 Radius=5 StartAngle=3.07278 EndAngle=3.61388
    g6: LineSegment [constr] StartX=24.2497 StartY=1.33422 StartZ=0 EndX=26.0308 EndY=2.24407 EndZ=0
    g7: ArcOfCircle CenterX=-4.3466 CenterY=-43.9012 CenterZ=0 NormalX=0 NormalY=0 NormalZ=1 AngleXU=0 Radius=3.90316 StartAngle=1.43923 EndAngle=1.59679
    g8: ArcOfCircle CenterX=0 CenterY=-11.0537 CenterZ=0 NormalX=0 NormalY=0 NormalZ=1 AngleXU=0 Radius=29.2307 StartAngle=4.58083 EndAngle=6.75547
  constraints (23):
    c: Radius(g0) = 2
    c: DistanceX(g0) = 23.5
    c: DistanceY(g0) = 5
    c: Tangent(g0,g1) = 1.5708
    c: Tangent(g1,g2) = -1.5708
    c: Tangent(g2,g3) = -1.5708
    c: Tangent(g3,g4) = 1.5708
    c: Coincident(g6,g5) = 1.5708
    c: Equal(g5,g1)
    c: Tangent(g5,g0) = 1.5708
    c: Equal(g3,g1)
    c: Radius(g5) = 5
    c: Equal(g4,g0)
    c: DistanceX(g4) = -4.5
    c: DistanceY(g4) = -38
    c: Coincident(g6,g1)
    c: Perpendicular(g2,g6)
    c: Distance(g6) = 2
    c: PointOnObject(g2,g-2)
    c: Coincident(g8,g2)
    c: Tangent(g8,g5) = 1.5708
    c: Tangent(g7,g4) = 1.5708
    c: Tangent(g7,g8) = 1.5708
FEATURE [PartDesign::Pad] Pad010
  Length = 20
  Length2 = 100
  Midplane = true
  Placement = pos=(0,0,0) rot=(0.57735,0.57735,0.57735;2.0944rad)
  Profile = -> Sketch052
  Type = 0
  expr: Length = Spreadsheet.Larg
FEATURE [PartDesign::Plane] DatumPlane006
  Length = 62.7511
  MapMode = 13
  Placement = pos=(3.33333,-3.49902,-37.7663) rot=(0,0.834007,0.551754;3.14159rad)
  ResizeMode = 0
  Support = -> [Pad010]
  Width = 94.0459
FEATURE [Sketcher::SketchObject] Sketch053
  ExternalGeometry = -> [Pad010]
  MapMode = 5
  Placement = pos=(3.33333,-3.49902,-37.7663) rot=(0,0.834007,0.551754;3.14159rad)
  Support = -> [DatumPlane006]
  sketch-geometry (4):
    g0: LineSegment StartX=-6.66667 StartY=-2.42629 StartZ=0 EndX=-6.41667 EndY=-2.42629 EndZ=0
    g1: LineSegment StartX=-6.41667 StartY=-2.42629 StartZ=0 EndX=-6.41667 EndY=1.57371 EndZ=0
    g2: LineSegment StartX=-6.41667 StartY=1.57371 StartZ=0 EndX=-6.66667 EndY=1.57371 EndZ=0
    g3: LineSegment StartX=-6.66667 StartY=1.57371 StartZ=0 EndX=-6.66667 EndY=-2.42629 EndZ=0
  constraints (11):
    c: Coincident(g0,g1)
    c: Coincident(g1,g2)
    c: Coincident(g2,g3)
    c: Coincident(g3,g0)
    c: Horizontal(g0)
    c: Horizontal(g2)
    c: Vertical(g1)
    c: Vertical(g3)
    c: Coincident(g0,g-3)
    c: DistanceX(g2,g2) = 0.25
    c: DistanceY(g3,g3) = 4
FEATURE [PartDesign::Plane] DatumPlane007
  Length = 62.4895
  MapMode = 13
  Placement = pos=(3.33333,25.4371,1.94079) rot=(0,0.972247,0.233955;3.14159rad)
  ResizeMode = 0
  Support = -> [Pad010]
  Width = 90.4829
FEATURE [Sketcher::SketchObject] Sketch054
  ExternalGeometry = -> [Pad010]
  MapMode = 5
  Placement = pos=(3.33333,25.4371,1.94079) rot=(0,0.972247,0.233955;3.14159rad)
  Support = -> [DatumPlane007]
  sketch-geometry (4):
    g0: LineSegment StartX=-6.66667 StartY=0.666667 StartZ=0 EndX=-6.61667 EndY=0.666667 EndZ=0
    g1: LineSegment StartX=-6.61667 StartY=0.666667 StartZ=0 EndX=-6.61667 EndY=-3.33333 EndZ=0
    g2: LineSegment StartX=-6.61667 StartY=-3.33333 StartZ=0 EndX=-6.66667 EndY=-3.33333 EndZ=0
    g3: LineSegment StartX=-6.66667 StartY=-3.33333 StartZ=0 EndX=-6.66667 EndY=0.666667 EndZ=0
  constraints (11):
    c: Coincident(g0,g1)
    c: Coincident(g1,g2)
    c: Coincident(g2,g3)
    c: Coincident(g3,g0)
    c: Horizontal(g0)
    c: Horizontal(g2)
    c: Vertical(g1)
    c: Vertical(g3)
    c: Coincident(g0,g-3)
    c: DistanceX(g0,g0) = 0.05
    c: DistanceY(g3,g3) = 4
FEATURE [PartDesign::SubtractivePipe] SubtractivePipe001
  AuxilleryCurvelinear = true
  AuxillerySpineTangent = false
  BaseFeature = -> Pad010
  Binormal = (0,0,0)
  Mode = 0
  Placement = pos=(0,0,0) rot=(0.57735,0.57735,0.57735;2.0944rad)
  Profile = -> Sketch053
  Sections = -> [Sketch054]
  Spine = -> Pad010 [Edge22,Edge24]
  SpineTangent = false
  Transformation = 1
  Transition = 0
FEATURE [PartDesign::Mirrored] Mirrored001
  BaseFeature = -> SubtractivePipe001
  MirrorPlane = -> YZ_Plane009
  Originals = -> [SubtractivePipe001]
  Placement = pos=(0,0,0) rot=(0.57735,0.57735,0.57735;2.0944rad)
FEATURE [PartDesign::Body] Body010  label="Leather_02"
  Group = -> [Sketch052,Pad010,DatumPlane006,Sketch053,DatumPlane007,Sketch054,SubtractivePipe001,Mirrored001]
  Origin = -> Origin009
  Tip = -> Mirrored001
FEATURE [Sketcher::SketchObject] Sketch055
  MapMode = 5
  Placement = pos=(0,0,0) rot=(0.57735,0.57735,0.57735;2.0944rad)
  Support = -> [YZ_Plane010]
  sketch-geometry (8):
    g0: LineSegment StartX=23.8941 StartY=-22.6359 StartZ=0 EndX=28.6952 EndY=-25.3191 EndZ=0
    g1: LineSegment StartX=28.6952 StartY=-25.3191 StartZ=0 EndX=27.2316 EndY=-27.9379 EndZ=0
    g2: LineSegment StartX=27.2316 StartY=-27.9379 StartZ=0 EndX=22.4305 EndY=-25.2546 EndZ=0
    g3: LineSegment StartX=23.8941 StartY=-22.6359 StartZ=0 EndX=22.4305 EndY=-25.2546 EndZ=0
    g4: LineSegment [constr] StartX=23.1623 StartY=-23.9452 StartZ=0 EndX=27.9634 EndY=-26.6285 EndZ=0
    g5: LineSegment [constr] StartX=23.8941 StartY=-22.6359 StartZ=0 EndX=23.8068 EndY=-22.5871 EndZ=0
    g6: LineSegment [constr] StartX=23.8941 StartY=-22.6359 StartZ=0 EndX=23.9429 EndY=-22.5486 EndZ=0
    g7: LineSegment [constr] StartX=0 StartY=-11 StartZ=0 EndX=23.1623 EndY=-23.9452 EndZ=0
  constraints (21):
    c: Coincident(g0,g1)
    c: Coincident(g1,g2)
    c: Coincident(g0,g3)
    c: Coincident(g3,g2)
    c: Perpendicular(g0,g3)
    c: Perpendicular(g1,g2)
    c: Perpendicular(g0,g1)
    c: Distance(g3) = 3
    c: Symmetric(g0,g1,g4)
    c: Symmetric(g0,g2,g4)
    c: Distance(g2) = 5.5
    c: Coincident(g5,g0)
    c: Coincident(g6,g0)
    c: Parallel(g0,g5)
    c: Parallel(g6,g3)
    c: Equal(g6,g5)
    c: Distance(g6) = 0.1
    c: PointOnObject(g7,g-2)
    c: Coincident(g7,g4)
    c: Parallel(g7,g4)
    c: DistanceY(g7) = -11
FEATURE [PartDesign::Pad] Pad011
  Length = 21
  Length2 = 100
  Midplane = true
  Placement = pos=(0,0,0) rot=(0.57735,0.57735,0.57735;2.0944rad)
  Profile = -> Sketch055
  Type = 0
  expr: Length = Spreadsheet.Larg + 1
FEATURE [Sketcher::SketchObject] Sketch056
  ExternalGeometry = -> [Pad011]
  MapMode = 5
  Placement = pos=(2e-16,-3.95275,-7.07247) rot=(-0.244427,-0.244427,-0.938355;1.63438rad)
  Support = -> [Pad011]
  sketch-geometry (11):
    g0: LineSegment StartX=-36.7009 StartY=10 StartZ=0 EndX=-32.6009 EndY=10 EndZ=0
    g1: LineSegment StartX=-32.4009 StartY=9.8 StartZ=0 EndX=-32.4009 EndY=-9.8 EndZ=0
    g2: LineSegment StartX=-32.6009 StartY=-10 StartZ=0 EndX=-36.7009 EndY=-10 EndZ=0
    g3: LineSegment StartX=-36.9009 StartY=-9.8 StartZ=0 EndX=-36.9009 EndY=9.8 EndZ=0
    g4: GeomPoint X=-34.6509 Y=1.09e-14 Z=0
    g5: ArcOfCircle CenterX=-36.7009 CenterY=9.8 CenterZ=0 NormalX=0 NormalY=0 NormalZ=1 AngleXU=0 Radius=0.2 StartAngle=1.5708 EndAngle=3.14159
    g6: ArcOfCircle CenterX=-32.6009 CenterY=9.8 CenterZ=0 NormalX=0 NormalY=0 NormalZ=1 AngleXU=0 Radius=0.2 StartAngle=2.3e-15 EndAngle=1.5708
    g7: ArcOfCircle CenterX=-32.6009 CenterY=-9.8 CenterZ=0 NormalX=0 NormalY=0 NormalZ=1 AngleXU=0 Radius=0.2 StartAngle=4.71239 EndAngle=6.28319
    g8: ArcOfCircle CenterX=-36.7009 CenterY=-9.8 CenterZ=0 NormalX=0 NormalY=0 NormalZ=1 AngleXU=0 Radius=0.2 StartAngle=3.14159 EndAngle=4.71239
    g9: LineSegment [constr] StartX=-36.7009 StartY=-10 StartZ=0 EndX=-36.7009 EndY=-10.5 EndZ=0
    g10: LineSegment [constr] StartX=-36.9009 StartY=-9.8 StartZ=0 EndX=-37.4009 EndY=-9.8 EndZ=0
  constraints (26):
    c: Horizontal(g0)
    c: Horizontal(g2)
    c: Vertical(g1)
    c: Vertical(g3)
    c: Symmetric(g-4,g-3,g4)
    c: Tangent(g3,g5) = 1.5708
    c: Tangent(g0,g5) = 1.5708
    c: Tangent(g0,g6) = 1.5708
    c: Tangent(g1,g6) = 1.5708
    c: Tangent(g1,g7) = 1.5708
    c: Tangent(g2,g7) = 1.5708
    c: Tangent(g2,g8) = 1.5708
    c: Tangent(g3,g8) = 1.5708
    c: Equal(g8,g7)
    c: Equal(g7,g5)
    c: Equal(g5,g6)
    c: Radius(g5) = 0.2
    c: DistanceY(g-4,g2) = 0.5
    c: Coincident(g9,g2)
    c: Coincident(g10,g3)
    c: PointOnObject(g10,g-4)
    c: Horizontal(g10)
    c: Horizontal(g9,g-4)
    c: Vertical(g9)
    c: Equal(g10,g9)
    c: Symmetric(g7,g5,g4)
FEATURE [PartDesign::Pocket] Pocket010
  BaseFeature = -> Pad011
  Length = 5
  Length2 = 100
  Placement = pos=(0,0,0) rot=(0.57735,0.57735,0.57735;2.0944rad)
  Profile = -> Sketch056
  Type = 0
FEATURE [PartDesign::Fillet] Fillet005
  Base = -> Pocket010 [Edge18,Edge15,Edge16,Edge14]
  BaseFeature = -> Pocket010
  Placement = pos=(0,0,0) rot=(0.57735,0.57735,0.57735;2.0944rad)
  Radius = 1
  SupportTransform = true
FEATURE [PartDesign::Body] Body011  label="Leather_Retainer"
  Group = -> [Sketch055,Pad011,Sketch056,Pocket010,Fillet005]
  Origin = -> Origin010
  Tip = -> Fillet005
FEATURE [Spreadsheet::Sheet] Spreadsheet
  cells = E2=Entre axe; F2(EntreAxe)=47; E3=Hauteur; F3(Haut)=5; E4=Largeur; F4(Larg)=20; E5=EpaisseurNato; F5(EpaisNato)=1; E6=EpaisseurLeather; F6(EpaisLeather)=2
FEATURE [Mesh::Feature] case_420
FEATURE [Sketcher::SketchObject] Sketch058
  MapMode = 5
  Placement = pos=(0,0,0) rot=(1,0,0;1.5708rad)
  Support = -> [XZ_Plane006]
  sketch-geometry (4):
    g0: LineSegment StartX=10.5 StartY=-40 StartZ=0 EndX=30.5 EndY=-40 EndZ=0
    g1: LineSegment StartX=30.5 StartY=-40 StartZ=0 EndX=30.5 EndY=-45 EndZ=0
    g2: LineSegment StartX=30.5 StartY=-45 StartZ=0 EndX=10.5 EndY=-45 EndZ=0
    g3: LineSegment StartX=10.5 StartY=-45 StartZ=0 EndX=10.5 EndY=-40 EndZ=0
  constraints (12):
    c: Coincident(g0,g1)
    c: Coincident(g1,g2)
    c: Coincident(g2,g3)
    c: Coincident(g3,g0)
    c: Horizontal(g0)
    c: Horizontal(g2)
    c: Vertical(g1)
    c: Vertical(g3)
    c: DistanceY(g3,g3) = 5
    c: DistanceX(g0,g0) = 20
    c: DistanceX(g0) = 10.5
    c: DistanceY(g2) = -45
FEATURE [PartDesign::Point] DatumPoint
  AttacherType = Attacher::AttachEnginePoint
  MapMode = 37
  Placement = pos=(1.64e-14,29.3862,-22.1881) rot=(0,0,1;0rad)
  Support = -> [Pad007]
FEATURE [PartDesign::Plane] DatumPlane008
  AttachmentOffset = pos=(0,0,-1) rot=(0,0,1;0rad)
  Length = 62.5353
  MapMode = 13
  Placement = pos=(6.66667,29.1017,-21.0204) rot=(1,0,0;2.79253rad)
  ResizeMode = 0
  Support = -> [DatumPoint,Pad007]
  Width = 91.1025
FEATURE [Sketcher::SketchObject] Sketch057
  ExternalGeometry = -> [Pad007]
  MapMode = 5
  Placement = pos=(6.66667,29.1017,-21.0204) rot=(1,0,0;2.79253rad)
  Support = -> [DatumPlane008]
  sketch-geometry (4):
    g0: LineSegment StartX=-12.7346 StartY=5 StartZ=0 EndX=7.26538 EndY=5 EndZ=0
    g1: LineSegment StartX=7.26538 StartY=5 StartZ=0 EndX=7.26538 EndY=-5 EndZ=0
    g2: LineSegment StartX=7.26538 StartY=-5 StartZ=0 EndX=-12.7346 EndY=-5 EndZ=0
    g3: LineSegment StartX=-12.7346 StartY=-5 StartZ=0 EndX=-12.7346 EndY=5 EndZ=0
  constraints (11):
    c: Coincident(g0,g1)
    c: Coincident(g1,g2)
    c: Coincident(g2,g3)
    c: Coincident(g3,g0)
    c: Horizontal(g0)
    c: Horizontal(g2)
    c: Vertical(g3)
    c: DistanceY(g3,g3) = 10
    c: DistanceX(g0,g0) = 20
    c: DistanceX(g2,g-3) = 5
    c: Symmetric(g0,g1,g-1)
FEATURE [PartDesign::SubtractivePipe] SubtractivePipe
  AuxilleryCurvelinear = true
  AuxillerySpineTangent = false
  BaseFeature = -> Pad007
  Binormal = (0,0,0)
  Mode = 0
  Placement = pos=(0,0,0) rot=(0.57735,0.57735,0.57735;2.0944rad)
  Profile = -> Sketch057
  Sections = -> [Sketch058]
  Spine = -> Pad007 [Edge13,Edge10,Edge7]
  SpineTangent = false
  Transformation = 1
  Transition = 0
FEATURE [PartDesign::Mirrored] Mirrored
  BaseFeature = -> SubtractivePipe
  MirrorPlane = -> YZ_Plane006
  Originals = -> [SubtractivePipe]
  Placement = pos=(0,0,0) rot=(0.57735,0.57735,0.57735;2.0944rad)
FEATURE [PartDesign::Body] Body007  label="Leather_1"
  Group = -> [Sketch041,Pad007,Sketch057,Sketch058,DatumPoint,DatumPlane008,SubtractivePipe,Mirrored]
  Origin = -> Origin006
  Tip = -> Mirrored
FEATURE [Part::Cut] Cut  label="Leather_01"
  Base = -> Body007
  Tool = -> Array
FEATURE [App::DocumentObjectGroup] Group  label="Leather"
  Group = -> [Cut,Body008,Body009,Body010,Body011]
FEATURE [PartDesign::Fillet] Fillet
  Base = -> Pocket004 [Edge75,Edge22]
  BaseFeature = -> Pocket004
  Placement = pos=(0,0,0) rot=(0.57735,0.57735,0.57735;2.0944rad)
  Radius = 5
  SupportTransform = true
FEATURE [PartDesign::Body] Body001  label="Nato"
  Group = -> [Sketch031,Pad,Sketch039,Pocket004,Fillet]
  Origin = -> Origin001
  Tip = -> Fillet
FEATURE [App::DocumentObjectGroup] Group001  label="Nato001"
  Group = -> [Body001,Body,Body004,Body005,Body006]
FEATURE [Sketcher::SketchObject] Sketch059
  MapMode = 5
  Placement = pos=(0,0,0) rot=(0.57735,0.57735,0.57735;2.0944rad)
  Support = -> [YZ_Plane011]
  expr: Constraints[1] = Spreadsheet.Haut
  expr: Constraints[0] = -Spreadsheet.EntreAxe / 2
  sketch-geometry (12):
    g0: GeomPoint X=-23.5 Y=5 Z=0
    g1: ArcOfCircle CenterX=-14.4787 CenterY=-10.795 CenterZ=0 NormalX=0 NormalY=0 NormalZ=1 AngleXU=0 Radius=20 StartAngle=1.94981 EndAngle=2.24332
    g2: LineSegment StartX=-24.1904 StartY=2.91907 StartZ=0 EndX=-20.8406 EndY=5.01225 EndZ=0
    g3: ArcOfCircle CenterX=-21.6937 CenterY=7.32116 CenterZ=0 NormalX=0 NormalY=0 NormalZ=1 AngleXU=0 Radius=0.5 StartAngle=0.558505 EndAngle=1.94981
    g4: LineSegment StartX=-21.2697 StartY=7.58612 StartZ=0 EndX=-20.5224 EndY=6.39022 EndZ=0
    g5: ArcOfCircle CenterX=-21.3705 CenterY=5.8603 CenterZ=0 NormalX=0 NormalY=0 NormalZ=1 AngleXU=0 Radius=1 StartAngle=5.27089 EndAngle=6.84169
    g6: ArcOfCircle CenterX=-26.6265 CenterY=4.45893 CenterZ=0 NormalX=0 NormalY=0 NormalZ=1 AngleXU=0 Radius=0.5 StartAngle=2.24332 EndAngle=3.7001
    g7: LineSegment StartX=-27.0506 StartY=4.19397 StartZ=0 EndX=-26.6018 EndY=3.4758 EndZ=0
    g8: ArcOfCircle CenterX=-25.1177 CenterY=4.40316 CenterZ=0 NormalX=0 NormalY=0 NormalZ=1 AngleXU=0 Radius=1.75 StartAngle=3.7001 EndAngle=5.27089
    g9: LineSegment [constr] StartX=-20.8406 StartY=5.01225 StartZ=0 EndX=-22.4303 EndY=7.5564 EndZ=0
    g10: LineSegment [constr] StartX=-24.1904 StartY=2.91907 StartZ=0 EndX=-25.8861 EndY=5.63283 EndZ=0
    g11: LineSegment [constr] StartX=-20.5224 StartY=6.39022 StartZ=0 EndX=-26.2044 EndY=2.83976 EndZ=0
  constraints (30):
    c: DistanceX(g0) = -23.5
    c: DistanceY(g0) = 5
    c: Tangent(g1,g3) = -1.5708
    c: Tangent(g3,g4) = 1.5708
    c: Tangent(g4,g5) = 1.5708
    c: Tangent(g1,g6) = -1.5708
    c: Tangent(g6,g7) = -1.5708
    c: Tangent(g7,g8) = -1.5708
    c: Tangent(g2,g8) = -1.5708
    c: Tangent(g2,g5) = -1.5708
    c: Equal(g6,g3)
    c: Radius(g3) = 0.5
    c: Parallel(g7,g4)
    c: Coincident(g9,g2)
    c: PointOnObject(g9,g1)
    c: Coincident(g10,g2)
    c: PointOnObject(g10,g1)
    c: Perpendicular(g9,g2)
    c: Distance(g9) = 3
    c: Parallel(g9,g4)
    c: Distance(g10) = 3.2
    c: Angle(g2) = 0.558505
    c: Parallel(g10,g9)
    c: Coincident(g11,g4)
    c: PointOnObject(g11,g7)
    c: Perpendicular(g4,g11)
    c: Distance(g11) = 6.7
    c: Radius(g5) = 1
    c: Radius(g8) = 1.75
    c: Radius(g1) = 20
FEATURE [PartDesign::Pad] Pad012
  Length = 20
  Length2 = 100
  Midplane = true
  Placement = pos=(0,0,0) rot=(0.57735,0.57735,0.57735;2.0944rad)
  Profile = -> Sketch059
  Type = 0
  expr: Length = Spreadsheet.Larg
FEATURE [Sketcher::SketchObject] Sketch061
  ExternalGeometry = -> [Pad012]
  MapMode = 5
  Placement = pos=(-7.2e-15,-8.10482,12.9704) rot=(0.693005,0.693005,0.198716;3.53391rad)
  Support = -> [Pad012]
  sketch-geometry (8):
    g0: LineSegment StartX=-20.7177 StartY=10 StartZ=0 EndX=-17.3677 EndY=10 EndZ=0
    g1: LineSegment StartX=-17.3677 StartY=10 StartZ=0 EndX=-17.3677 EndY=4.5 EndZ=0
    g2: LineSegment StartX=-17.3677 StartY=4.5 StartZ=0 EndX=-20.7177 EndY=4.5 EndZ=0
    g3: LineSegment StartX=-20.7177 StartY=4.5 StartZ=0 EndX=-20.7177 EndY=10 EndZ=0
    g4: LineSegment StartX=-20.7177 StartY=-10 StartZ=0 EndX=-17.3677 EndY=-10 EndZ=0
    g5: LineSegment StartX=-17.3677 StartY=-10 StartZ=0 EndX=-17.3677 EndY=-4.5 EndZ=0
    g6: LineSegment StartX=-17.3677 StartY=-4.5 StartZ=0 EndX=-20.7177 EndY=-4.5 EndZ=0
    g7: LineSegment StartX=-20.7177 StartY=-4.5 StartZ=0 EndX=-20.7177 EndY=-10 EndZ=0
  constraints (19):
    c: Coincident(g0,g1)
    c: Coincident(g1,g2)
    c: Coincident(g2,g3)
    c: Coincident(g3,g0)
    c: Horizontal(g0)
    c: Horizontal(g2)
    c: Vertical(g1)
    c: Vertical(g3)
    c: Coincident(g0,g-3)
    c: Coincident(g4,g5)
    c: Coincident(g5,g6)
    c: Coincident(g6,g7)
    c: Coincident(g7,g4)
    c: Vertical(g5)
    c: Coincident(g4,g-3)
    c: Symmetric(g6,g2,g-1)
    c: Symmetric(g4,g-4,g4)
    c: Symmetric(g5,g1,g-1)
    c: DistanceY(g5,g1) = 9
FEATURE [PartDesign::Pocket] Pocket011
  BaseFeature = -> Pad012
  Length = 5
  Length2 = 100
  Placement = pos=(0,0,0) rot=(0.57735,0.57735,0.57735;2.0944rad)
  Profile = -> Sketch061
  Type = 1
FEATURE [Sketcher::SketchObject] Sketch063
  ExternalGeometry = -> [Pocket011]
  MapMode = 5
  Placement = pos=(4.5,-6e-16,2.4e-15) rot=(0.57735,0.57735,0.57735;2.0944rad)
  Support = -> [Pocket011]
  sketch-geometry (1):
    g0: ArcOfCircle CenterX=-14.4787 CenterY=-10.795 CenterZ=0 NormalX=0 NormalY=0 NormalZ=1 AngleXU=0 Radius=20 StartAngle=1.92889 EndAngle=2.26565
  constraints (5):
    c: Equal(g0,g-3)
    c: PointOnObject(g0,g-6)
    c: PointOnObject(g0,g-5)
    c: PointOnObject(g-3,g0)
    c: PointOnObject(g-4,g0)
FEATURE [PartDesign::Plane] DatumPlane
  Length = 83.5509
  MapMode = 8
  Placement = pos=(4.5,-26.938,4.85005) rot=(-0.669302,0.669302,-0.322596;3.76571rad)
  ResizeMode = 0
  Support = -> [Pocket011]
  Width = 61.9654
FEATURE [Sketcher::SketchObject] Sketch062
  MapMode = 5
  Placement = pos=(4.5,-26.938,4.85005) rot=(-0.669302,0.669302,-0.322596;3.76571rad)
  Support = -> [DatumPlane]
  sketch-geometry (3):
    g0: LineSegment StartX=0 StartY=-0.025 StartZ=0 EndX=0 EndY=0.025 EndZ=0
    g1: LineSegment StartX=0 StartY=0.025 StartZ=0 EndX=-0.0433013 EndY=0 EndZ=0
    g2: LineSegment StartX=-0.0433013 StartY=0 StartZ=0 EndX=0 EndY=-0.025 EndZ=0
  constraints (9):
    c: PointOnObject(g0,g-2)
    c: Vertical(g0)
    c: Coincident(g0,g1)
    c: Coincident(g1,g2)
    c: Coincident(g2,g0)
    c: Equal(g1,g2)
    c: Equal(g2,g0)
    c: Horizontal(g1,g-1)
    c: DistanceY(g0,g0) = 0.05
FEATURE [PartDesign::SubtractivePipe] SubtractivePipe002
  AuxilleryCurvelinear = true
  AuxillerySpineTangent = false
  BaseFeature = -> Pocket011
  Binormal = (0,0,0)
  Mode = 0
  Placement = pos=(0,0,0) rot=(0.57735,0.57735,0.57735;2.0944rad)
  Profile = -> Sketch062
  Spine = -> Sketch063
  SpineTangent = false
  Transformation = 0
  Transition = 0
FEATURE [PartDesign::Mirrored] Mirrored002
  BaseFeature = -> SubtractivePipe002
  MirrorPlane = -> YZ_Plane011
  Originals = -> [SubtractivePipe002]
  Placement = pos=(0,0,0) rot=(0.57735,0.57735,0.57735;2.0944rad)
FEATURE [PartDesign::Body] Body012
  Group = -> [Sketch059,Pad012,Sketch061,Pocket011,Sketch062,Sketch063,DatumPlane,SubtractivePipe002,Mirrored002]
  Origin = -> Origin011
  Tip = -> Mirrored002
FEATURE [App::DocumentObjectGroup] Group002  label="Stainless"
  Group = -> [Body012]
FEATURE [Sketcher::SketchObject] Sketch064
  MapMode = 5
  Placement = pos=(0,0,0) rot=(0.57735,0.57735,0.57735;2.0944rad)
  Support = -> [YZ_Plane012]
  expr: Constraints[0] = -Spreadsheet.EntreAxe / 2
  expr: Constraints[1] = Spreadsheet.Haut
  sketch-geometry (12):
    g0: GeomPoint X=-23.5 Y=5 Z=0
    g1: ArcOfCircle CenterX=-10.5686 CenterY=-7.43473 CenterZ=0 NormalX=0 NormalY=0 NormalZ=1 AngleXU=0 Radius=20 StartAngle=2.44021 EndAngle=3.08761
    g2: LineSegment StartX=-27.1207 StartY=-6.11499 StartZ=0 EndX=-23.4782 EndY=3.89274 EndZ=0
    g3: ArcOfCircle CenterX=-25.4656 CenterY=5.14819 CenterZ=0 NormalX=0 NormalY=0 NormalZ=1 AngleXU=0 Radius=0.5 StartAngle=1.22173 EndAngle=2.44021
    g4: LineSegment StartX=-25.2946 StartY=5.61803 StartZ=0 EndX=-24.0759 EndY=5.17445 EndZ=0
    g5: ArcOfCircle CenterX=-24.4179 CenterY=4.23476 CenterZ=0 NormalX=0 NormalY=0 NormalZ=1 AngleXU=0 Radius=1 StartAngle=5.93412 EndAngle=7.50492
    g6: ArcOfCircle CenterX=-30.0402 CenterY=-6.3826 CenterZ=0 NormalX=0 NormalY=0 NormalZ=1 AngleXU=0 Radius=0.5 StartAngle=3.08761 EndAngle=4.36332
    g7: LineSegment StartX=-30.2112 StartY=-6.85244 StartZ=0 EndX=-29.3637 EndY=-7.16092 EndZ=0
    g8: ArcOfCircle CenterX=-28.7652 CenterY=-5.51645 CenterZ=0 NormalX=0 NormalY=0 NormalZ=1 AngleXU=0 Radius=1.75 StartAngle=4.36332 EndAngle=5.93412
    g9: LineSegment [constr] StartX=-23.4782 StartY=3.89274 StartZ=0 EndX=-26.2973 EndY=4.9188 EndZ=0
    g10: LineSegment [constr] StartX=-27.1207 StartY=-6.11499 StartZ=0 EndX=-30.4096 EndY=-4.91792 EndZ=0
    g11: LineSegment [constr] StartX=-24.0759 StartY=5.17445 StartZ=0 EndX=-28.6589 EndY=-7.41743 EndZ=0
  constraints (30):
    c: DistanceX(g0) = -23.5
    c: DistanceY(g0) = 5
    c: Tangent(g1,g3) = -1.5708
    c: Tangent(g3,g4) = 1.5708
    c: Tangent(g4,g5) = 1.5708
    c: Tangent(g1,g6) = -1.5708
    c: Tangent(g6,g7) = -1.5708
    c: Tangent(g7,g8) = -1.5708
    c: Tangent(g2,g8) = -1.5708
    c: Tangent(g2,g5) = -1.5708
    c: Equal(g6,g3)
    c: Radius(g3) = 0.5
    c: Parallel(g7,g4)
    c: Coincident(g9,g2)
    c: PointOnObject(g9,g1)
    c: Coincident(g10,g2)
    c: PointOnObject(g10,g1)
    c: Perpendicular(g9,g2)
    c: Distance(g9) = 3
    c: Parallel(g9,g4)
    c: Distance(g10) = 3.5
    c: Angle(g2) = 1.22173
    c: Parallel(g10,g9)
    c: Coincident(g11,g4)
    c: PointOnObject(g11,g7)
    c: Perpendicular(g4,g11)
    c: Distance(g11) = 13.4
    c: Radius(g5) = 1
    c: Radius(g8) = 1.75
    c: Radius(g1) = 20
FEATURE [PartDesign::Pad] Pad013
  Length = 20
  Length2 = 100
  Midplane = true
  Placement = pos=(0,0,0) rot=(0.57735,0.57735,0.57735;2.0944rad)
  Profile = -> Sketch064
  Type = 0
  expr: Length = Spreadsheet.Larg
FEATURE [Sketcher::SketchObject] Sketch065
  ExternalGeometry = -> [Pad013]
  MapMode = 5
  Placement = pos=(-1.29e-14,-21.9829,8.00111) rot=(0.633687,0.633687,0.443713;3.97682rad)
  Support = -> [Pad013]
  sketch-geometry (12):
    g0: LineSegment StartX=-16.772 StartY=10 StartZ=0 EndX=-12.272 EndY=10 EndZ=0
    g1: LineSegment StartX=-12.272 StartY=10 StartZ=0 EndX=-12.272 EndY=4.5 EndZ=0
    g2: LineSegment StartX=-12.272 StartY=4.5 StartZ=0 EndX=-16.772 EndY=4.5 EndZ=0
    g3: LineSegment StartX=-16.772 StartY=4.5 StartZ=0 EndX=-16.772 EndY=10 EndZ=0
    g4: LineSegment StartX=-16.772 StartY=-10 StartZ=0 EndX=-12.272 EndY=-10 EndZ=0
    g5: LineSegment StartX=-12.272 StartY=-10 StartZ=0 EndX=-12.272 EndY=-4.5 EndZ=0
    g6: LineSegment StartX=-12.272 StartY=-4.5 StartZ=0 EndX=-16.772 EndY=-4.5 EndZ=0
    g7: LineSegment StartX=-16.772 StartY=-4.5 StartZ=0 EndX=-16.772 EndY=-10 EndZ=0
    g8: LineSegment StartX=-3.37204 StartY=4.5 StartZ=0 EndX=-6.77204 EndY=4.5 EndZ=0
    g9: LineSegment StartX=-6.77204 StartY=4.5 StartZ=0 EndX=-6.77204 EndY=-4.5 EndZ=0
    g10: LineSegment StartX=-6.77204 StartY=-4.5 StartZ=0 EndX=-3.37204 EndY=-4.5 EndZ=0
    g11: LineSegment StartX=-3.37204 StartY=-4.5 StartZ=0 EndX=-3.37204 EndY=4.5 EndZ=0
  constraints (32):
    c: Coincident(g0,g1)
    c: Coincident(g1,g2)
    c: Coincident(g2,g3)
    c: Coincident(g3,g0)
    c: Horizontal(g0)
    c: Horizontal(g2)
    c: Vertical(g1)
    c: Vertical(g3)
    c: Coincident(g0,g-3)
    c: Coincident(g4,g5)
    c: Coincident(g5,g6)
    c: Coincident(g6,g7)
    c: Coincident(g7,g4)
    c: Vertical(g5)
    c: Coincident(g4,g-3)
    c: Symmetric(g6,g2,g-1)
    c: Symmetric(g5,g1,g-1)
    c: DistanceY(g5,g1) = 9
    c: Horizontal(g4,g-4)
    c: DistanceX(g4,g4) = 4.5
    c: Coincident(g8,g9)
    c: Coincident(g9,g10)
    c: Coincident(g10,g11)
    c: Coincident(g11,g8)
    c: Horizontal(g8)
    c: Horizontal(g10)
    c: Vertical(g9)
    c: Vertical(g11)
    c: PointOnObject(g8,g-4)
    c: Horizontal(g8,g1)
    c: Horizontal(g5,g9)
    c: DistanceX(g6,g9) = 10
FEATURE [PartDesign::Pocket] Pocket012
  BaseFeature = -> Pad013
  Length = 5
  Length2 = 100
  Placement = pos=(0,0,0) rot=(0.57735,0.57735,0.57735;2.0944rad)
  Profile = -> Sketch065
  Type = 1
FEATURE [PartDesign::Plane] DatumPlane009
  Length = 67.0914
  MapMode = 8
  Placement = pos=(4.5,-30.5395,-6.35562) rot=(-0.706978,0.706978,-0.019087;3.17976rad)
  ResizeMode = 0
  Support = -> [Pocket012]
  Width = 60.6268
FEATURE [Sketcher::SketchObject] Sketch066
  MapMode = 5
  Placement = pos=(4.5,-30.5395,-6.35562) rot=(-0.706978,0.706978,-0.019087;3.17976rad)
  Support = -> [DatumPlane009]
  sketch-geometry (3):
    g0: LineSegment StartX=0 StartY=-0.025 StartZ=0 EndX=0 EndY=0.025 EndZ=0
    g1: LineSegment StartX=0 StartY=0.025 StartZ=0 EndX=-0.0433013 EndY=0 EndZ=0
    g2: LineSegment StartX=-0.0433013 StartY=0 StartZ=0 EndX=0 EndY=-0.025 EndZ=0
  constraints (9):
    c: PointOnObject(g0,g-2)
    c: Vertical(g0)
    c: Coincident(g0,g1)
    c: Coincident(g1,g2)
    c: Coincident(g2,g0)
    c: Equal(g1,g2)
    c: Equal(g2,g0)
    c: Horizontal(g1,g-1)
    c: DistanceY(g0,g0) = 0.05
FEATURE [Sketcher::SketchObject] Sketch067
  ExternalGeometry = -> [Pocket012]
  MapMode = 5
  Placement = pos=(4.5,-2.7e-15,1.4e-15) rot=(0.57735,0.57735,0.57735;2.0944rad)
  Support = -> [Pocket012]
  sketch-geometry (1):
    g0: ArcOfCircle CenterX=-10.5686 CenterY=-7.43473 CenterZ=0 NormalX=0 NormalY=0 NormalZ=1 AngleXU=0 Radius=20 StartAngle=2.4227 EndAngle=3.10619
  constraints (5):
    c: Equal(g-7,g0)
    c: PointOnObject(g0,g-8)
    c: PointOnObject(g0,g-9)
    c: PointOnObject(g-7,g0)
    c: PointOnObject(g-6,g0)
FEATURE [PartDesign::SubtractivePipe] SubtractivePipe003
  AuxilleryCurvelinear = true
  AuxillerySpineTangent = false
  BaseFeature = -> Pocket012
  Binormal = (0,0,0)
  Mode = 0
  Placement = pos=(0,0,0) rot=(0.57735,0.57735,0.57735;2.0944rad)
  Profile = -> Sketch066
  Spine = -> Sketch067
  SpineTangent = false
  Transformation = 0
  Transition = 0
FEATURE [PartDesign::Mirrored] Mirrored003
  BaseFeature = -> SubtractivePipe003
  MirrorPlane = -> YZ_Plane012
  Originals = -> [SubtractivePipe003]
  Placement = pos=(0,0,0) rot=(0.57735,0.57735,0.57735;2.0944rad)
FEATURE [PartDesign::Body] Body013
  Group = -> [Sketch064,Pad013,Sketch065,Pocket012,Sketch066,Sketch067,DatumPlane009,SubtractivePipe003,Mirrored003]
  Origin = -> Origin012
  Tip = -> Mirrored003
FEATURE [Sketcher::SketchObject] Sketch068
  MapMode = 5
  Placement = pos=(0,0,0) rot=(0.57735,0.57735,0.57735;2.0944rad)
  Support = -> [YZ_Plane013]
  expr: Constraints[1] = Spreadsheet.Haut
  expr: Constraints[0] = -Spreadsheet.EntreAxe / 2
  sketch-geometry (12):
    g0: GeomPoint X=-23.5 Y=5 Z=0
    g1: ArcOfCircle CenterX=-0.904002 CenterY=-16.0053 CenterZ=0 NormalX=0 NormalY=0 NormalZ=1 AngleXU=0 Radius=20 StartAngle=1.21848 EndAngle=1.86588
    g2: LineSegment StartX=-5.325 StartY=0 StartZ=0 EndX=5.325 EndY=0 EndZ=0
    g3: ArcOfCircle CenterX=5.825 CenterY=2.29695 CenterZ=0 NormalX=0 NormalY=0 NormalZ=1 AngleXU=0 Radius=0.5 StartAngle=0 EndAngle=1.21848
    g4: LineSegment StartX=6.325 StartY=2.29695 StartZ=0 EndX=6.325 EndY=1 EndZ=0
    g5: ArcOfCircle CenterX=5.325 CenterY=1 CenterZ=0 NormalX=0 NormalY=0 NormalZ=1 AngleXU=0 Radius=1 StartAngle=4.71239 EndAngle=6.28319
    g6: ArcOfCircle CenterX=-6.575 CenterY=2.65191 CenterZ=0 NormalX=0 NormalY=0 NormalZ=1 AngleXU=0 Radius=0.5 StartAngle=1.86588 EndAngle=3.14159
    g7: LineSegment StartX=-7.075 StartY=2.65191 StartZ=0 EndX=-7.075 EndY=1.75 EndZ=0
    g8: ArcOfCircle CenterX=-5.325 CenterY=1.75 CenterZ=0 NormalX=0 NormalY=0 NormalZ=1 AngleXU=0 Radius=1.75 StartAngle=3.14159 EndAngle=4.71239
    g9: LineSegment [constr] StartX=5.325 StartY=0 StartZ=0 EndX=5.325 EndY=3 EndZ=0
    g10: LineSegment [constr] StartX=-5.325 StartY=0 StartZ=0 EndX=-5.325 EndY=3.5 EndZ=0
    g11: LineSegment [constr] StartX=6.325 StartY=1 StartZ=0 EndX=-7.075 EndY=1 EndZ=0
  constraints (31):
    c: DistanceX(g0) = -23.5
    c: DistanceY(g0) = 5
    c: Tangent(g1,g3) = -1.5708
    c: Tangent(g3,g4) = 1.5708
    c: Tangent(g4,g5) = 1.5708
    c: Tangent(g1,g6) = -1.5708
    c: Tangent(g6,g7) = -1.5708
    c: Tangent(g7,g8) = -1.5708
    c: Tangent(g2,g8) = -1.5708
    c: Tangent(g2,g5) = -1.5708
    c: Equal(g6,g3)
    c: Radius(g3) = 0.5
    c: Parallel(g7,g4)
    c: Coincident(g9,g2)
    c: PointOnObject(g9,g1)
    c: Coincident(g10,g2)
    c: PointOnObject(g10,g1)
    c: Perpendicular(g9,g2)
    c: Distance(g9) = 3
    c: Parallel(g9,g4)
    c: Distance(g10) = 3.5
    c: Parallel(g10,g9)
    c: Coincident(g11,g4)
    c: PointOnObject(g11,g7)
    c: Perpendicular(g4,g11)
    c: Distance(g11) = 13.4
    c: Radius(g5) = 1
    c: Radius(g8) = 1.75
    c: Radius(g1) = 20
    c: Horizontal(g2)
    c: Symmetric(g2,g2,g-1)
FEATURE [PartDesign::Pad] Pad014
  Length = 20
  Length2 = 100
  Midplane = true
  Placement = pos=(0,0,0) rot=(0.57735,0.57735,0.57735;2.0944rad)
  Profile = -> Sketch068
  Type = 0
  expr: Length = Spreadsheet.Larg
FEATURE [Sketcher::SketchObject] Sketch070
  ExternalGeometry = -> [Pad014]
  MapMode = 5
  Placement = pos=(0,0,0) rot=(0.707107,0.707107,0;3.14159rad)
  Support = -> [Pad014]
  sketch-geometry (12):
    g0: LineSegment StartX=-7.075 StartY=10 StartZ=0 EndX=-2.575 EndY=10 EndZ=0
    g1: LineSegment StartX=-2.575 StartY=10 StartZ=0 EndX=-2.575 EndY=4.5 EndZ=0
    g2: LineSegment StartX=-2.575 StartY=4.5 StartZ=0 EndX=-7.075 EndY=4.5 EndZ=0
    g3: LineSegment StartX=-7.075 StartY=4.5 StartZ=0 EndX=-7.075 EndY=10 EndZ=0
    g4: LineSegment StartX=-7.075 StartY=-10 StartZ=0 EndX=-2.575 EndY=-10 EndZ=0
    g5: LineSegment StartX=-2.575 StartY=-10 StartZ=0 EndX=-2.575 EndY=-4.5 EndZ=0
    g6: LineSegment StartX=-2.575 StartY=-4.5 StartZ=0 EndX=-7.075 EndY=-4.5 EndZ=0
    g7: LineSegment StartX=-7.075 StartY=-4.5 StartZ=0 EndX=-7.075 EndY=-10 EndZ=0
    g8: LineSegment StartX=6.325 StartY=4.5 StartZ=0 EndX=2.925 EndY=4.5 EndZ=0
    g9: LineSegment StartX=2.925 StartY=4.5 StartZ=0 EndX=2.925 EndY=-4.5 EndZ=0
    g10: LineSegment StartX=2.925 StartY=-4.5 StartZ=0 EndX=6.325 EndY=-4.5 EndZ=0
    g11: LineSegment StartX=6.325 StartY=-4.5 StartZ=0 EndX=6.325 EndY=4.5 EndZ=0
  constraints (32):
    c: Coincident(g0,g1)
    c: Coincident(g1,g2)
    c: Coincident(g2,g3)
    c: Coincident(g3,g0)
    c: Horizontal(g0)
    c: Horizontal(g2)
    c: Vertical(g1)
    c: Vertical(g3)
    c: Coincident(g0,g-3)
    c: Coincident(g4,g5)
    c: Coincident(g5,g6)
    c: Coincident(g6,g7)
    c: Coincident(g7,g4)
    c: Vertical(g5)
    c: Coincident(g4,g-3)
    c: Symmetric(g6,g2,g-1)
    c: Symmetric(g5,g1,g-1)
    c: DistanceY(g5,g1) = 9
    c: Horizontal(g4,g-4)
    c: DistanceX(g4,g4) = 4.5
    c: Coincident(g8,g9)
    c: Coincident(g9,g10)
    c: Coincident(g10,g11)
    c: Coincident(g11,g8)
    c: Horizontal(g8)
    c: Horizontal(g10)
    c: Vertical(g9)
    c: Vertical(g11)
    c: PointOnObject(g8,g-4)
    c: Horizontal(g8,g1)
    c: Horizontal(g5,g9)
    c: DistanceX(g6,g9) = 10
FEATURE [PartDesign::Pocket] Pocket013
  BaseFeature = -> Pad014
  Length = 5
  Length2 = 100
  Placement = pos=(0,0,0) rot=(0.57735,0.57735,0.57735;2.0944rad)
  Profile = -> Sketch070
  Type = 1
FEATURE [PartDesign::Plane] DatumPlane010
  Length = 73.5495
  MapMode = 8
  Placement = pos=(4.5,-6.72041,3.1303) rot=(-0.626298,0.626298,-0.464222;4.01083rad)
  ResizeMode = 0
  Support = -> [Pocket013]
  Width = 61.1696
FEATURE [Sketcher::SketchObject] Sketch069
  ExternalGeometry = -> [Pocket013]
  MapMode = 5
  Placement = pos=(4.5,-1e-15,3.2e-15) rot=(0.57735,0.57735,0.57735;2.0944rad)
  Support = -> [Pocket013]
  sketch-geometry (1):
    g0: ArcOfCircle CenterX=-0.904002 CenterY=-16.0053 CenterZ=0 NormalX=0 NormalY=0 NormalZ=1 AngleXU=0 Radius=20 StartAngle=1.20097 EndAngle=1.88446
  constraints (5):
    c: Equal(g-7,g0)
    c: PointOnObject(g0,g-8)
    c: PointOnObject(g0,g-9)
    c: PointOnObject(g-7,g0)
    c: PointOnObject(g-6,g0)
FEATURE [Sketcher::SketchObject] Sketch071
  MapMode = 5
  Placement = pos=(4.5,-6.72041,3.1303) rot=(-0.626298,0.626298,-0.464222;4.01083rad)
  Support = -> [DatumPlane010]
  sketch-geometry (3):
    g0: LineSegment StartX=0 StartY=-0.025 StartZ=0 EndX=0 EndY=0.025 EndZ=0
    g1: LineSegment StartX=0 StartY=0.025 StartZ=0 EndX=-0.0433013 EndY=0 EndZ=0
    g2: LineSegment StartX=-0.0433013 StartY=0 StartZ=0 EndX=0 EndY=-0.025 EndZ=0
  constraints (9):
    c: PointOnObject(g0,g-2)
    c: Vertical(g0)
    c: Coincident(g0,g1)
    c: Coincident(g1,g2)
    c: Coincident(g2,g0)
    c: Equal(g1,g2)
    c: Equal(g2,g0)
    c: Horizontal(g1,g-1)
    c: DistanceY(g0,g0) = 0.05
FEATURE [PartDesign::SubtractivePipe] SubtractivePipe004
  AuxilleryCurvelinear = true
  AuxillerySpineTangent = false
  BaseFeature = -> Pocket013
  Binormal = (0,0,0)
  Mode = 0
  Placement = pos=(0,0,0) rot=(0.57735,0.57735,0.57735;2.0944rad)
  Profile = -> Sketch071
  Spine = -> Sketch069
  SpineTangent = false
  Transformation = 0
  Transition = 0
FEATURE [PartDesign::Mirrored] Mirrored004
  BaseFeature = -> SubtractivePipe004
  MirrorPlane = -> YZ_Plane013
  Originals = -> [SubtractivePipe004]
  Placement = pos=(0,0,0) rot=(0.57735,0.57735,0.57735;2.0944rad)
FEATURE [PartDesign::Body] Body014
  Group = -> [Sketch068,Pad014,Sketch070,Pocket013,Sketch071,Sketch069,DatumPlane010,SubtractivePipe004,Mirrored004]
  Origin = -> Origin013
  Placement = pos=(0,0,0) rot=(0,0,1;1.5708rad)
  Tip = -> Mirrored004
FEATURE [Sketcher::SketchObject] Sketch072
  Placement = pos=(0,0,0) rot=(0.57735,0.57735,0.57735;2.0944rad)
  sketch-geometry (1):
    g0: ArcOfCircle CenterX=0 CenterY=-10 CenterZ=0 NormalX=0 NormalY=0 NormalZ=1 AngleXU=0 Radius=27 StartAngle=3.14159 EndAngle=4.79966
  constraints (5):
    c: PointOnObject(g0,g-2)
    c: DistanceY(g0) = -10
    c: DistanceX(g0) = -27
    c: DistanceY(g0) = -10
    c: Angle(g0) = 1.65806
FEATURE [Part::FeaturePython] PathArray  # WARN: FeaturePython — macro-defined, semantics opaque (R4)
  Align = true
  Base = -> Body014
  Count = 6
  PathObj = -> Sketch072
  Xlate = (0,0,0)
